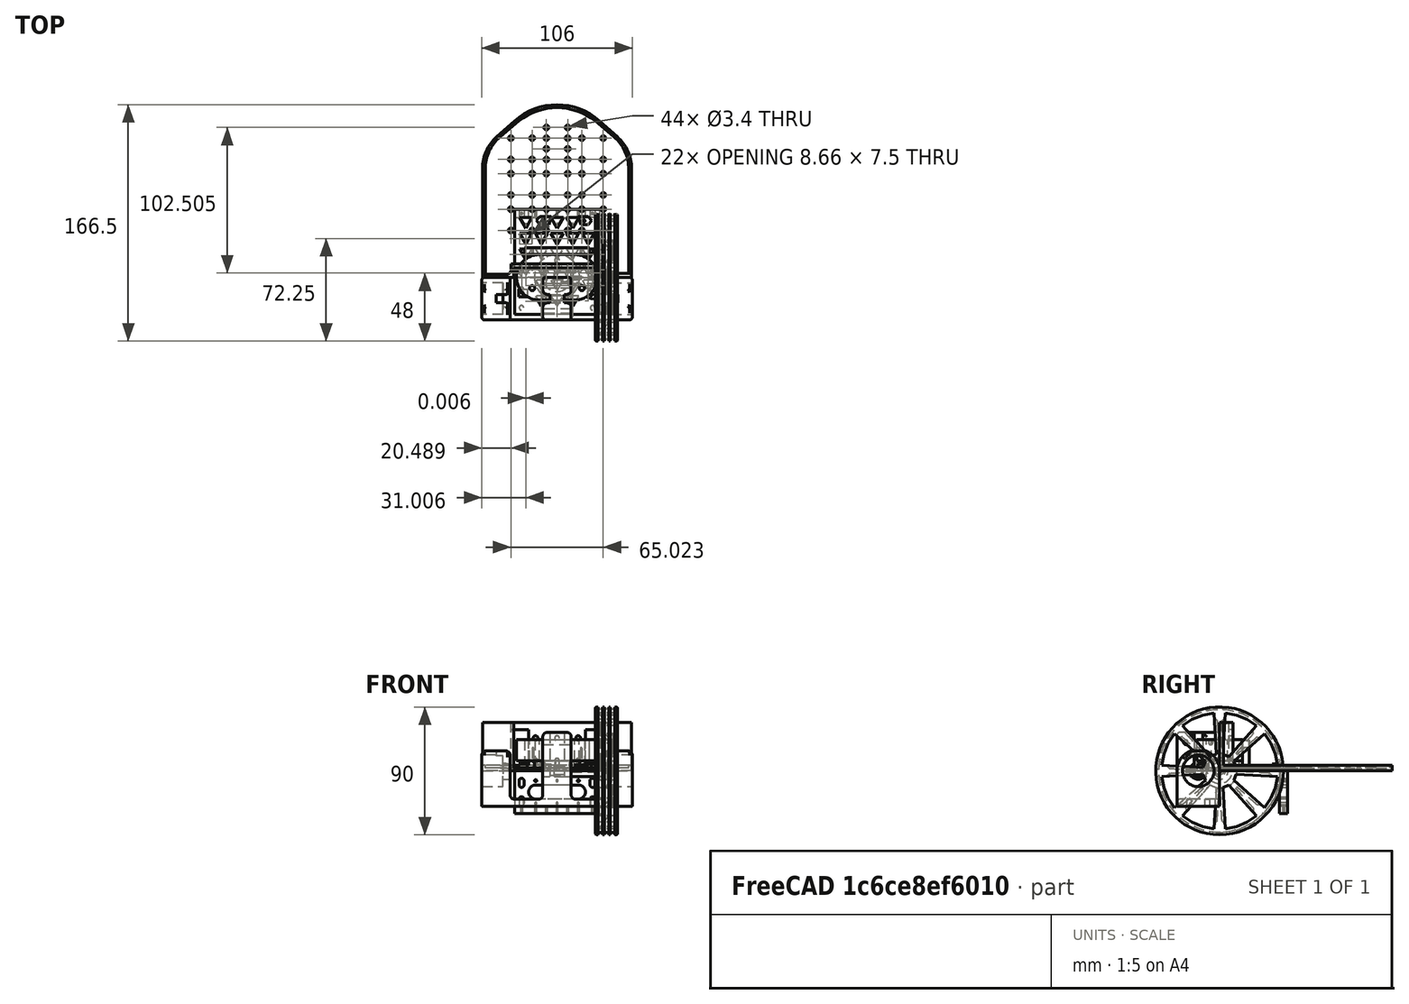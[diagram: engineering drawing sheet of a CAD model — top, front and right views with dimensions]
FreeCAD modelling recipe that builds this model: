
FCSTD DOCUMENT  (FreeCAD 0.18R4 (GitTag))
Label: MotoriGialliRuote90-r00
License: All rights reserved
LicenseURL: http://en.wikipedia.org/wiki/All_rights_reserved
objects: Sketcher::SketchObject×29, PartDesign::Pocket×17, PartDesign::Pad×11, PartDesign::Body×6, App::Part×6, PartDesign::Fillet×2, PartDesign::Revolution×1, PartDesign::FeatureBase×1, Mesh::Feature×1
note: 96 computed .brp shape members not serialized (recipe doc carries the construction recipe); baked Part::Feature solids carry a one-line shape summary decoded from their .brp

FEATURE [Sketcher::SketchObject] Sketch  label="ProfiloPrincipaleStaffa"
  MapMode = 5
  Placement = pos=(0,0,0) rot=(1,0,0;1.5708rad)
  Support = -> [XZ_Plane001]
  constraints (76):
    c: Vertical(g1)
    c: Horizontal(g2)
    c: Coincident(g3,g4)
    c: Horizontal(g4)
    c: Horizontal(g5)
    c: Vertical(g6)
    c: Equal(g5,g2)
    c: Vertical(g3)
    c: DistanceY(g3,g-1) = 20
    c: Horizontal(g7)
    c: DistanceX(g7,g7) = 20
    c: DistanceX(g7,g3) = 43
    c: Tangent(g0,g8) = 1.5708
    c: Tangent(g1,g8) = 1.5708
    c: Tangent(g0,g9) = 1.5708
    c: Tangent(g6,g9) = 1.5708
    c: Equal(g9,g8)
    c: Radius(g9) = 3
    c: DistanceY(g-1,g0) = 27
    c: Tangent(g5,g10) = -1.5708
    c: Tangent(g6,g10) = -1.5708
    c: Tangent(g1,g11) = -1.5708
    c: Tangent(g2,g11) = -1.5708
    c: Equal(g11,g10)
    c: Equal(g10,g9)
    c: Coincident(g7,g6)
    c: Coincident(g7,g1)
    c: Coincident(g12,g5)
    c: PointOnObject(g12,g4)
    c: Vertical(g12)
    c: DistanceY(g12,g5) = 5
    c: Vertical(g13)
    c: Horizontal(g14)
    c: Coincident(g15,g3)
    c: Vertical(g15)
    c: Tangent(g2,g16) = -1.5708
    c: Tangent(g13,g16) = -1.5708
    c: Equal(g16,g11)
    c: Coincident(g17,g1)
    c: Coincident(g17,g13)
    c: DistanceX(g17,g17) = 23
    c: Symmetric(g0,g0,g-2)
    c: Tangent(g13,g18) = 1.5708
    c: Tangent(g14,g18) = 1.5708
    c: Tangent(g14,g19) = 1.5708
    c: Tangent(g15,g19) = 1.5708
    c: Equal(g19,g18)
    c: Equal(g18,g16)
    c: Coincident(g20,g13)
    c: Coincident(g20,g15)
    c: Vertical(g21)
    c: Horizontal(g22)
    c: Vertical(g23)
    c: Coincident(g23,g24)
    c: Vertical(g24)
    c: Coincident(g24,g4)
    c: Tangent(g23,g25) = -1.5708
    c: Tangent(g22,g25) = -1.5708
    c: Tangent(g22,g26) = -1.5708
    c: Tangent(g21,g26) = -1.5708
    c: Tangent(g21,g27) = 1.5708
    c: Tangent(g5,g27) = -1.5708
    c: Equal(g27,g26)
    c: Equal(g26,g25)
    c: Equal(g25,g10)
    c: Coincident(g28,g21)
    c: Coincident(g28,g13)
    c: Horizontal(g28)
    c: Equal(g14,g22)
    c: Coincident(g29,g23)
    c: Coincident(g29,g5)
    c: Horizontal(g29)
    c: Coincident(g30,g2)
    c: Coincident(g30,g3)
    c: Horizontal(g30)
    c: DistanceY(g-1,g14) = 14
FEATURE [PartDesign::Pad] Pad  label="ProfiloPrincipaleStaffa001"
  Length = 30
  Length2 = 100
  Placement = pos=(0,0,0) rot=(1,0,0;1.5708rad)
  Profile = -> Sketch
  Type = 0
FEATURE [PartDesign::Pocket] Pocket  label="Unnamed001"
  Length = 100
  Length2 = 100
  Type = 0
FEATURE [Sketcher::SketchObject] Sketch002  label="Unnamed002"
FEATURE [PartDesign::Pocket] Pocket001  label="Unnamed003"
  Length = 100
  Length2 = 100
  Type = 0
FEATURE [Sketcher::SketchObject] Sketch003  label="Unnamed004"
FEATURE [PartDesign::Pocket] Pocket002  label="Unnamed005"
  Length = 100
  Length2 = 100
  Type = 0
FEATURE [Sketcher::SketchObject] Sketch001  label="ScontornoSupportoCuscinettiSX"
  MapMode = 5
  Placement = pos=(-53,0,0) rot=(0.707107,0,-0.707107;3.14159rad)
  Support = -> [Pocket002]
  constraints (97):
    c: Coincident(g0,g1)
    c: Coincident(g11,g2)
    c: Coincident(g2,g3)
    c: Coincident(g10,g0)
    c: Horizontal(g0)
    c: Horizontal(g2)
    c: Vertical(g1)
    c: Vertical(g3)
    c: Horizontal(g4)
    c: Coincident(g4,g5)
    c: Vertical(g5)
    c: Coincident(g5,g6)
    c: Horizontal(g6)
    c: Horizontal(g7)
    c: Coincident(g7,g8)
    c: Vertical(g8)
    c: Coincident(g8,g9)
    c: Equal(g8,g5)
    c: DistanceY(g8,g7) = 6
    c: Tangent(g3,g10)
    c: Tangent(g1,g11)
    c: Horizontal(g9)
    c: Tangent(g7,g12) = 1.5708
    c: Tangent(g10,g12) = -1.5708
    c: Tangent(g9,g13) = 1.5708
    c: Tangent(g3,g13) = -1.5708
    c: Tangent(g11,g14) = -1.5708
    c: Tangent(g6,g14) = -1.5708
    c: Tangent(g4,g15) = -1.5708
    c: Tangent(g1,g15) = -1.5708
    c: Equal(g15,g12)
    c: Equal(g12,g13)
    c: Radius(g12) = 3
    c: Equal(g10,g11)
    c: Equal(g11,g3)
    c: Equal(g1,g10)
    c: DistanceX(g0,g4) = 5
    c: DistanceX(g7,g0) = 10
    c: DistanceX(g2,g2) = 23
    c: DistanceX(g5,g-1) = 5
    c: Coincident(g16,g1)
    c: Coincident(g17,g16)
    c: Coincident(g17,g11)
    c: Vertical(g17)
    c: Equal(g17,g16)
    c: DistanceY(g-1,g16) = 15
    c: Coincident(g18,g19)
    c: Coincident(g29,g20)
    c: Coincident(g20,g21)
    c: Coincident(g28,g18)
    c: Horizontal(g18)
    c: Horizontal(g20)
    c: Vertical(g19)
    c: Vertical(g21)
    c: Horizontal(g22)
    c: Coincident(g22,g23)
    c: Vertical(g23)
    c: Coincident(g23,g24)
    c: Horizontal(g24)
    c: Horizontal(g25)
    c: Coincident(g25,g26)
    c: Vertical(g26)
    c: Coincident(g26,g27)
    c: Equal(g26,g23)
    c: Tangent(g21,g28)
    c: Tangent(g19,g29)
    c: Horizontal(g27)
    c: Tangent(g25,g30) = 1.5708
    c: Tangent(g28,g30) = -1.5708
    c: Tangent(g27,g31) = 1.5708
    c: Tangent(g21,g31) = -1.5708
    c: Tangent(g29,g32) = -1.5708
    c: Tangent(g24,g32) = -1.5708
    c: Tangent(g22,g33) = -1.5708
    c: Tangent(g19,g33) = -1.5708
    c: Equal(g33,g30)
    c: Equal(g30,g31)
    c: Radius(g30) = 3
    c: Equal(g28,g29)
    c: Equal(g29,g21)
    c: Equal(g19,g28)
    c: Coincident(g34,g19)
    c: Coincident(g35,g34)
    c: Coincident(g35,g29)
    c: Vertical(g35)
    c: Equal(g35,g34)
    c: Equal(g26,g5)
    c: Equal(g20,g0)
    c: Equal(g21,g1)
    c: DistanceY(g2,g0) = 20
    c: Coincident(g36,g16)
    c: PointOnObject(g36,g-2)
    c: Horizontal(g36)
    c: Coincident(g37,g36)
    c: Coincident(g37,g34)
    c: Horizontal(g37)
    c: Equal(g36,g37)
FEATURE [Sketcher::SketchObject] Sketch004  label="Unnamed006"
FEATURE [PartDesign::Pocket] Pocket003  label="StaffaMotori004"
  BaseFeature = -> Pocket002
  Length = 25
  Length2 = 100
  Placement = pos=(0,0,0) rot=(1,0,0;1.5708rad)
  Profile = -> Sketch004
  Type = 0
FEATURE [PartDesign::Fillet] Fillet  label="StaffaMotori005"
  Base = -> Pocket003 [Edge114,Edge123]
  BaseFeature = -> Pocket003
  Placement = pos=(0,0,0) rot=(1,0,0;1.5708rad)
  Radius = 2
FEATURE [PartDesign::Pocket] Pocket004  label="Unnamed007"
  Length = 100
  Length2 = 100
  Type = 0
FEATURE [Sketcher::SketchObject] Sketch005  label="ScassoSedeCuscinettiRuotaDX"
  MapMode = 5
  Placement = pos=(53,0,0) rot=(0.707107,0,0.707107;3.14159rad)
  Support = -> [Pocket004]
  sketch-geometry (1):
    g0: Circle CenterX=0 CenterY=15 CenterZ=0 NormalX=0 NormalY=0 NormalZ=1 AngleXU=0 Radius=11.1
  constraints (3):
    c: PointOnObject(g0,g-2)
    c: Radius(g0) = 11.1
    c: DistanceY(g-1,g0) = 15
FEATURE [Sketcher::SketchObject] Sketch006  label="Unnamed008"
FEATURE [PartDesign::Pocket] Pocket005  label="StaffaMotori007"
  BaseFeature = -> Pocket004
  Length = 15
  Length2 = 100
  Placement = pos=(0,0,0) rot=(1,0,0;1.5708rad)
  Profile = -> Sketch006
  Type = 0
FEATURE [PartDesign::Pocket] Pocket006  label="Unnamed009"
  Length = 100
  Length2 = 100
  Type = 0
FEATURE [Sketcher::SketchObject] Sketch007  label="ForoMozzoRuotaSX"
  MapMode = 5
  Placement = pos=(-38,0,0) rot=(0.707107,0,-0.707107;3.14159rad)
  Support = -> [Pocket006]
  sketch-geometry (1):
    g0: Circle CenterX=0 CenterY=15 CenterZ=0 NormalX=0 NormalY=0 NormalZ=1 AngleXU=0 Radius=6
  constraints (3):
    c: PointOnObject(g0,g-2)
    c: Radius(g0) = 6
    c: DistanceY(g-1,g0) = 15
FEATURE [Sketcher::SketchObject] Sketch008  label="Unnamed010"
FEATURE [PartDesign::Pocket] Pocket007  label="StaffaMotori009"
  BaseFeature = -> Pocket006
  Length = 10
  Length2 = 100
  Placement = pos=(0,0,0) rot=(1,0,0;1.5708rad)
  Profile = -> Sketch008
  Type = 0
FEATURE [PartDesign::Pocket] Pocket008  label="Unnamed011"
  Length = 100
  Length2 = 100
  Type = 0
FEATURE [Sketcher::SketchObject] Sketch009  label="ForiFissaggioStaffaMotori"
  MapMode = 5
  Placement = pos=(0,-1.3e-14,-20) rot=(0,0,1;3.14159rad)
  Support = -> [Pocket008]
  sketch-geometry (4):
    g0: Circle CenterX=-20 CenterY=6.25 CenterZ=0 NormalX=0 NormalY=0 NormalZ=1 AngleXU=0 Radius=1.6
    g1: LineSegment StartX=-20 StartY=15 StartZ=0 EndX=-20 EndY=6.25 EndZ=0
    g2: Circle CenterX=25 CenterY=21.5 CenterZ=0 NormalX=0 NormalY=0 NormalZ=1 AngleXU=0 Radius=1.6
    g3: Circle CenterX=-25 CenterY=8.5 CenterZ=0 NormalX=0 NormalY=0 NormalZ=1 AngleXU=0 Radius=1.6
  constraints (11):
    c: Coincident(g2,g0)
    c: Vertical(g2)
    c: Coincident(g3,g2)
    c: Vertical(g3)
    c: Equal(g2,g3)
    c: DistanceY(g-1,g2) = 15
    c: Coincident(g1,g3)
    c: DistanceY(g1,g0) = 17.5
    c: Equal(g0,g1)
    c: Radius(g0) = 1.6
    c: DistanceX(g1,g-1) = 20
FEATURE [Sketcher::SketchObject] Sketch010  label="Unnamed012"
FEATURE [PartDesign::Pocket] Pocket009  label="StaffaMotori011"
  BaseFeature = -> Pocket008
  Length = 7
  Length2 = 100
  Placement = pos=(0,0,0) rot=(1,0,0;1.5708rad)
  Profile = -> Sketch010
  Type = 0
FEATURE [PartDesign::Body] Body  label="StaffaMotori"
  Group = -> [Sketch,Pad,Sketch001,Pocket,Sketch002,Pocket001,Sketch003,Pocket002,Sketch004,Pocket003,Fillet,Sketch005,Pocket004,Sketch006,Pocket005,Sketch007,Pocket006,Sketch008,Pocket007,Sketch009,Pocket008,Sketch010,Pocket009]
  Origin = -> Origin001
  Tip = -> Pocket009
FEATURE [App::Part] Part  label="Staffa Motori"
  Group = -> [Body]
  Origin = -> Origin
  Placement = pos=(0,0,15) rot=(1,0,0;1.5708rad)
FEATURE [Sketcher::SketchObject] Sketch011  label="ProfiloCerchione90asse8"
  MapMode = 5
  Placement = pos=(0,0,0) rot=(1,0,0;1.5708rad)
  Support = -> [XZ_Plane003]
  constraints (107):
    c: Vertical(g0)
    c: Coincident(g0,g1)
    c: Horizontal(g1)
    c: Coincident(g1,g2)
    c: Vertical(g2)
    c: Coincident(g2,g3)
    c: Horizontal(g3)
    c: Vertical(g4)
    c: Coincident(g5,g6)
    c: Vertical(g6)
    c: Vertical(g7)
    c: Coincident(g7,g8)
    c: Vertical(g9)
    c: Horizontal(g10)
    c: Coincident(g0,g10)
    c: Equal(g12,g13)
    c: Equal(g13,g11)
    c: Radius(g11) = 1.6
    c: Coincident(g14,g11)
    c: Coincident(g15,g12)
    c: Coincident(g16,g12)
    c: Coincident(g16,g13)
    c: Coincident(g17,g11)
    c: Horizontal(g14)
    c: Equal(g17,g14)
    c: Horizontal(g17)
    c: Coincident(g17,g13)
    c: Equal(g17,g16)
    c: Equal(g16,g15)
    c: Horizontal(g16)
    c: Horizontal(g15)
    c: Tangent(g6,g18) = -1.5708
    c: Tangent(g14,g18) = -1.5708
    c: Tangent(g7,g19) = -1.5708
    c: Tangent(g15,g19) = -1.5708
    c: Equal(g19,g18)
    c: Radius(g18) = 1
    c: Coincident(g20,g11)
    c: Coincident(g20,g11)
    c: Coincident(g21,g13)
    c: Coincident(g21,g13)
    c: Horizontal(g21)
    c: Coincident(g22,g12)
    c: Coincident(g22,g12)
    c: Horizontal(g22)
    c: Horizontal(g20)
    c: PointOnObject(g11,g20)
    c: PointOnObject(g13,g21)
    c: PointOnObject(g12,g22)
    c: Equal(g14,g15)
    c: DistanceX(g6,g11) = 2
    c: Equal(g6,g7)
    c: Coincident(g23,g5)
    c: Coincident(g23,g7)
    c: Horizontal(g24)
    c: Tangent(g4,g25) = 1.5708
    c: Tangent(g5,g25) = 1.5708
    c: Tangent(g9,g26) = 1.5708
    c: Tangent(g8,g26) = 1.5708
    c: Coincident(g24,g5)
    c: Coincident(g24,g8)
    c: Coincident(g27,g4)
    c: Coincident(g27,g9)
    c: Radius(g25) = 5
    c: DistanceY(g14,g5) = 2
    c: Coincident(g28,g25)
    c: Coincident(g28,g4)
    c: Coincident(g29,g9)
    c: Coincident(g29,g26)
    c: Coincident(g30,g26)
    c: Coincident(g30,g7)
    c: Vertical(g30)
    c: Coincident(g31,g25)
    c: Coincident(g31,g5)
    c: Equal(g28,g29)
    c: Equal(g31,g30)
    c: DistanceY(g15,g26) = 9
    c: PointOnObject(g32,g9)
    c: Horizontal(g32)
    c: Radius(g33) = 3
    c: Coincident(g10,g33)
    c: PointOnObject(g10,g-1)
    c: PointOnObject(g33,g-1)
    c: Coincident(g9,g33)
    c: Coincident(g34,g33)
    c: Coincident(g34,g9)
    c: Vertical(g34)
    c: Coincident(g35,g33)
    c: Coincident(g35,g10)
    c: DistanceY(g15,g-1) = 45
    c: Tangent(g3,g36) = 1.5708
    c: Tangent(g4,g36) = 1.5708
    c: Radius(g36) = 3
    c: DistanceY(g0,g0) = 4.1
    c: DistanceY(g2,g0) = 6
    c: DistanceX(g0,g2) = 29
    c: DistanceX(g3,g3) = 2
    c: Coincident(g32,g4)
    c: Coincident(g10,g37)
    c: PointOnObject(g37,g-1)
    c: Coincident(g37,g38)
    c: Coincident(g38,g7)
    c: Vertical(g38)
    c: DistanceX(g0,g-1) = 2
    c: Coincident(g39,g36)
    c: Coincident(g39,g25)
    c: Radius(g39) = 16
FEATURE [PartDesign::Revolution] Revolution  label="RuoteDa90asse009"
  Angle = 360
  Axis = (1,0,0)
  Base = (0,0,0)
  Placement = pos=(0,0,0) rot=(1,0,0;1.5708rad)
  Profile = -> Sketch011
  ReferenceAxis = -> Sketch011 [H_Axis]
  Reversed = true
FEATURE [Sketcher::SketchObject] Sketch013  label="AllegerimentoRuota"
  MapMode = 5
  Placement = pos=(42.6,0,0) rot=(0.707107,0,0.707107;3.14159rad)
  Support = -> [Revolution]
  sketch-geometry (6):
    g0: ArcOfCircle CenterX=0 CenterY=-0.8 CenterZ=0 NormalX=0 NormalY=0 NormalZ=1 AngleXU=0 Radius=2.4 StartAngle=3.14159 EndAngle=6.28319
    g1: LineSegment StartX=2.4 StartY=0.8 StartZ=0 EndX=2.4 EndY=-0.8 EndZ=0
    g2: LineSegment StartX=0 StartY=0 StartZ=0 EndX=0 EndY=-0.8 EndZ=0
    g3: LineSegment StartX=11.7694 StartY=-2.34108 StartZ=0 EndX=11.7694 EndY=2.34108 EndZ=0
    g4: LineSegment StartX=9.97764 StartY=6.66684 StartZ=0 EndX=6.66684 EndY=9.97764 EndZ=0
    g5: LineSegment StartX=2.34108 StartY=11.7694 StartZ=0 EndX=-2.34108 EndY=11.7694 EndZ=0
  constraints (14):
    c: Tangent(g0,g3) = 1.5708
    c: Tangent(g0,g2) = -1.5708
    c: Tangent(g2,g1) = -1.5708
    c: Tangent(g3,g1) = 1.5708
    c: Vertical(g2)
    c: Equal(g0,g1)
    c: Radius(g0) = 2.4
    c: DistanceY(g1,g0) = 1.6
    c: Coincident(g4,g0)
    c: Vertical(g4)
    c: Coincident(g5,g4)
    c: Equal(g5,g4)
    c: Coincident(g5,g1)
    c: Coincident(g-1,g4)
FEATURE [Sketcher::SketchObject] Sketch017  label="Unnamed013"
FEATURE [PartDesign::Pocket] Pocket014  label="RuoteDa90asse014"
  BaseFeature = -> Revolution
  Length = 15000
  Length2 = 100
  Placement = pos=(0,0,0) rot=(1,0,0;1.5708rad)
  Profile = -> Sketch017
  Type = 0
FEATURE [PartDesign::Fillet] Fillet001  label="RuoteDa90asse015"
  Base = -> Pocket014 [Edge19,Edge21,Edge23,Edge25,Edge17,Edge27,Edge29,Edge31,Edge33,Edge35,Edge37,Edge39,Edge41,Edge11,Edge13,Edge15,Edge14,Edge18,Edge22,Edge26,Edge30,Edge34,Edge38,Edge10]
  BaseFeature = -> Pocket014
  Placement = pos=(0,0,0) rot=(1,0,0;1.5708rad)
  Radius = 2
FEATURE [PartDesign::Pocket] Pocket015  label="RuoteDa90asse016"
  BaseFeature = -> Fillet001
  Length = 12
  Length2 = 100
  Placement = pos=(0,0,0) rot=(1,0,0;1.5708rad)
  Profile = -> Sketch013
  Type = 0
FEATURE [PartDesign::FeatureBase] Clone
  BaseFeature = -> Pocket015
  Placement = pos=(0,0,0) rot=(1,0,0;1.5708rad)
FEATURE [PartDesign::Body] Body002
  BaseFeature = -> Pocket015
  Group = -> [Clone]
  Origin = -> Origin004
  Tip = -> Clone
FEATURE [App::Part] Part002  label="Ruote da 90 asse 8DX"
  Group = -> [Body002]
  Origin = -> Origin005
  Placement = pos=(27,0,0) rot=(0,0,1;0rad)
FEATURE [Sketcher::SketchObject] Sketch018  label="PortaArduinoSopraMotori001"
  MapMode = 5
  Support = -> [XY_Plane007]
  constraints (429):
    c: Coincident(g0,g1)
    c: Coincident(g1,g2)
    c: Coincident(g2,g3)
    c: Coincident(g3,g0)
    c: Horizontal(g2)
    c: Vertical(g1)
    c: Vertical(g3)
    c: Symmetric(g0,g0,g-2)
    c: DistanceX(g0,g0) = 60
    c: DistanceY(g1,g-1) = 26
    c: DistanceY(g1,g0) = 74
    c: Coincident(g4,g5)
    c: Coincident(g5,g6)
    c: Coincident(g6,g4)
    c: Equal(g4,g5)
    c: Equal(g4,g6)
    c: PointOnObject(g4,g7)
    c: PointOnObject(g5,g7)
    c: PointOnObject(g6,g7)
    c: Radius(g7) = 5
    c: Horizontal(g4)
    c: Coincident(g8,g9)
    c: Coincident(g9,g10)
    c: Coincident(g10,g8)
    c: Equal(g8,g9)
    c: Equal(g8,g10)
    c: PointOnObject(g8,g11)
    c: PointOnObject(g9,g11)
    c: PointOnObject(g10,g11)
    c: Equal(g7,g11) = 5
    c: Horizontal(g8)
    c: Coincident(g4,g12)
    c: Coincident(g8,g12)
    c: Distance(g12) = 11
    c: Angle(g12) = 0.000544822
    c: Coincident(g13,g14)
    c: Coincident(g14,g15)
    c: Coincident(g15,g13)
    c: Equal(g13,g14)
    c: Equal(g13,g15)
    c: PointOnObject(g13,g16)
    c: PointOnObject(g14,g16)
    c: PointOnObject(g15,g16)
    c: Equal(g7,g16) = 5
    c: Horizontal(g13)
    c: Coincident(g8,g17)
    c: Coincident(g13,g17)
    c: Equal(g12,g17)
    c: Parallel(g17,g12)
    c: Coincident(g18,g19)
    c: Coincident(g19,g20)
    c: Coincident(g20,g18)
    c: Equal(g18,g19)
    c: Equal(g18,g20)
    c: PointOnObject(g18,g21)
    c: PointOnObject(g19,g21)
    c: PointOnObject(g20,g21)
    c: Equal(g7,g21) = 5
    c: Horizontal(g18)
    c: Coincident(g13,g22)
    c: Coincident(g18,g22)
    c: Equal(g12,g22)
    c: Parallel(g22,g12)
    c: Coincident(g23,g24)
    c: Coincident(g24,g25)
    c: Coincident(g25,g23)
    c: Equal(g23,g24)
    c: Equal(g23,g25)
    c: PointOnObject(g23,g26)
    c: PointOnObject(g24,g26)
    c: PointOnObject(g25,g26)
    c: Equal(g7,g26) = 5
    c: Horizontal(g23)
    c: Coincident(g18,g27)
    c: Coincident(g23,g27)
    c: Equal(g12,g27)
    c: Parallel(g27,g12)
    c: Coincident(g28,g29)
    c: Coincident(g29,g30)
    c: Coincident(g30,g28)
    c: Equal(g28,g29)
    c: Equal(g28,g30)
    c: PointOnObject(g28,g31)
    c: PointOnObject(g29,g31)
    c: PointOnObject(g30,g31)
    c: Equal(g7,g31) = 5
    c: Horizontal(g28)
    c: Coincident(g4,g32)
    c: Coincident(g28,g32)
    c: Equal(g32,g12)
    c: Perpendicular(g32,g12)
    c: Coincident(g33,g34)
    c: Coincident(g34,g35)
    c: Coincident(g35,g33)
    c: Equal(g33,g34)
    c: Equal(g33,g35)
    c: PointOnObject(g33,g36)
    c: PointOnObject(g34,g36)
    c: PointOnObject(g35,g36)
    c: Equal(g7,g36) = 5
    c: Horizontal(g33)
    c: Coincident(g28,g37)
    c: Coincident(g33,g37)
    c: Equal(g12,g37)
    c: Parallel(g37,g12)
    c: Coincident(g38,g39)
    c: Coincident(g39,g40)
    c: Coincident(g40,g38)
    c: Equal(g38,g39)
    c: Equal(g38,g40)
    c: PointOnObject(g38,g41)
    c: PointOnObject(g39,g41)
    c: PointOnObject(g40,g41)
    c: Equal(g7,g41) = 5
    c: Horizontal(g38)
    c: Coincident(g33,g42)
    c: Coincident(g38,g42)
    c: Equal(g12,g42)
    c: Parallel(g42,g12)
    c: Coincident(g43,g44)
    c: Coincident(g44,g45)
    c: Coincident(g45,g43)
    c: Equal(g43,g44)
    c: Equal(g43,g45)
    c: PointOnObject(g43,g46)
    c: PointOnObject(g44,g46)
    c: PointOnObject(g45,g46)
    c: Equal(g7,g46) = 5
    c: Horizontal(g43)
    c: Coincident(g38,g47)
    c: Coincident(g43,g47)
    c: Equal(g12,g47)
    c: Parallel(g47,g12)
    c: Coincident(g48,g49)
    c: Coincident(g49,g50)
    c: Coincident(g50,g48)
    c: Equal(g48,g49)
    c: Equal(g48,g50)
    c: PointOnObject(g48,g51)
    c: PointOnObject(g49,g51)
    c: PointOnObject(g50,g51)
    c: Equal(g7,g51) = 5
    c: Horizontal(g48)
    c: Coincident(g43,g52)
    c: Coincident(g48,g52)
    c: Equal(g12,g52)
    c: Parallel(g52,g12)
    c: Coincident(g53,g54)
    c: Coincident(g54,g55)
    c: Coincident(g55,g53)
    c: Equal(g53,g54)
    c: Equal(g53,g55)
    c: PointOnObject(g53,g56)
    c: PointOnObject(g54,g56)
    c: PointOnObject(g55,g56)
    c: Equal(g7,g56) = 5
    c: Horizontal(g53)
    c: Coincident(g28,g57)
    c: Coincident(g53,g57)
    c: Equal(g32,g57)
    c: Perpendicular(g57,g12)
    c: Coincident(g58,g59)
    c: Coincident(g59,g60)
    c: Coincident(g60,g58)
    c: Equal(g58,g59)
    c: Equal(g58,g60)
    c: PointOnObject(g58,g61)
    c: PointOnObject(g59,g61)
    c: PointOnObject(g60,g61)
    c: Equal(g7,g61) = 5
    c: Horizontal(g58)
    c: Coincident(g53,g62)
    c: Coincident(g58,g62)
    c: Equal(g12,g62)
    c: Parallel(g62,g12)
    c: Coincident(g63,g64)
    c: Coincident(g64,g65)
    c: Coincident(g65,g63)
    c: Equal(g63,g64)
    c: Equal(g63,g65)
    c: PointOnObject(g63,g66)
    c: PointOnObject(g64,g66)
    c: PointOnObject(g65,g66)
    c: Equal(g7,g66) = 5
    c: Horizontal(g63)
    c: Coincident(g58,g67)
    c: Coincident(g63,g67)
    c: Equal(g12,g67)
    c: Parallel(g67,g12)
    c: Coincident(g68,g69)
    c: Coincident(g69,g70)
    c: Coincident(g70,g68)
    c: Equal(g68,g69)
    c: Equal(g68,g70)
    c: PointOnObject(g68,g71)
    c: PointOnObject(g69,g71)
    c: PointOnObject(g70,g71)
    c: Equal(g7,g71) = 5
    c: Horizontal(g68)
    c: Coincident(g63,g72)
    c: Coincident(g68,g72)
    c: Equal(g12,g72)
    c: Parallel(g72,g12)
    c: Coincident(g73,g74)
    c: Coincident(g74,g75)
    c: Coincident(g75,g73)
    c: Equal(g73,g74)
    c: Equal(g73,g75)
    c: PointOnObject(g73,g76)
    c: PointOnObject(g74,g76)
    c: PointOnObject(g75,g76)
    c: Equal(g7,g76) = 5
    c: Horizontal(g73)
    c: Coincident(g68,g77)
    c: Coincident(g73,g77)
    c: Equal(g12,g77)
    c: Parallel(g77,g12)
    c: Coincident(g78,g79)
    c: Coincident(g79,g80)
    c: Coincident(g80,g78)
    c: Equal(g78,g79)
    c: Equal(g78,g80)
    c: PointOnObject(g78,g81)
    c: PointOnObject(g79,g81)
    c: PointOnObject(g80,g81)
    c: Equal(g7,g81) = 5
    c: Horizontal(g78)
    c: Coincident(g53,g82)
    c: Coincident(g78,g82)
    c: Equal(g32,g82)
    c: Perpendicular(g82,g12)
    c: Coincident(g83,g84)
    c: Coincident(g84,g85)
    c: Coincident(g85,g83)
    c: Equal(g83,g84)
    c: Equal(g83,g85)
    c: PointOnObject(g83,g86)
    c: PointOnObject(g84,g86)
    c: PointOnObject(g85,g86)
    c: Equal(g7,g86) = 5
    c: Horizontal(g83)
    c: Coincident(g78,g87)
    c: Coincident(g83,g87)
    c: Equal(g12,g87)
    c: Parallel(g87,g12)
    c: Coincident(g88,g89)
    c: Coincident(g89,g90)
    c: Coincident(g90,g88)
    c: Equal(g88,g89)
    c: Equal(g88,g90)
    c: PointOnObject(g88,g91)
    c: PointOnObject(g89,g91)
    c: PointOnObject(g90,g91)
    c: Equal(g7,g91) = 5
    c: Horizontal(g88)
    c: Coincident(g83,g92)
    c: Coincident(g88,g92)
    c: Equal(g12,g92)
    c: Parallel(g92,g12)
    c: Coincident(g93,g94)
    c: Coincident(g94,g95)
    c: Coincident(g95,g93)
    c: Equal(g93,g94)
    c: Equal(g93,g95)
    c: PointOnObject(g93,g96)
    c: PointOnObject(g94,g96)
    c: PointOnObject(g95,g96)
    c: Equal(g7,g96) = 5
    c: Horizontal(g93)
    c: Coincident(g88,g97)
    c: Coincident(g93,g97)
    c: Equal(g12,g97)
    c: Parallel(g97,g12)
    c: Coincident(g98,g99)
    c: Coincident(g99,g100)
    c: Coincident(g100,g98)
    c: Equal(g98,g99)
    c: Equal(g98,g100)
    c: PointOnObject(g98,g101)
    c: PointOnObject(g99,g101)
    c: PointOnObject(g100,g101)
    c: Equal(g7,g101) = 5
    c: Horizontal(g98)
    c: Coincident(g93,g102)
    c: Coincident(g98,g102)
    c: Equal(g12,g102)
    c: Parallel(g102,g12)
    c: Coincident(g103,g104)
    c: Coincident(g104,g105)
    c: Coincident(g105,g103)
    c: Equal(g103,g104)
    c: Equal(g103,g105)
    c: PointOnObject(g103,g106)
    c: PointOnObject(g104,g106)
    c: PointOnObject(g105,g106)
    c: Equal(g7,g106) = 5
    c: Horizontal(g103)
    c: Coincident(g78,g107)
    c: Coincident(g103,g107)
    c: Equal(g32,g107)
    c: Perpendicular(g107,g12)
    c: Coincident(g108,g109)
    c: Coincident(g109,g110)
    c: Coincident(g110,g108)
    c: Equal(g108,g109)
    c: Equal(g108,g110)
    c: PointOnObject(g108,g111)
    c: PointOnObject(g109,g111)
    c: PointOnObject(g110,g111)
    c: Equal(g7,g111) = 5
    c: Horizontal(g108)
    c: Coincident(g103,g112)
    c: Coincident(g108,g112)
    c: Equal(g12,g112)
    c: Parallel(g112,g12)
    c: Coincident(g113,g114)
    c: Coincident(g114,g115)
    c: Coincident(g115,g113)
    c: Equal(g113,g114)
    c: Equal(g113,g115)
    c: PointOnObject(g113,g116)
    c: PointOnObject(g114,g116)
    c: PointOnObject(g115,g116)
    c: Equal(g7,g116) = 5
    c: Horizontal(g113)
    c: Coincident(g108,g117)
    c: Coincident(g113,g117)
    c: Equal(g12,g117)
    c: Parallel(g117,g12)
    c: Coincident(g118,g119)
    c: Coincident(g119,g120)
    c: Coincident(g120,g118)
    c: Equal(g118,g119)
    c: Equal(g118,g120)
    c: PointOnObject(g118,g121)
    c: PointOnObject(g119,g121)
    c: PointOnObject(g120,g121)
    c: Equal(g7,g121) = 5
    c: Horizontal(g118)
    c: Coincident(g113,g122)
    c: Coincident(g118,g122)
    c: Equal(g12,g122)
    c: Parallel(g122,g12)
    c: Coincident(g123,g124)
    c: Coincident(g124,g125)
    c: Coincident(g125,g123)
    c: Equal(g123,g124)
    c: Equal(g123,g125)
    c: PointOnObject(g123,g126)
    c: PointOnObject(g124,g126)
    c: PointOnObject(g125,g126)
    c: Equal(g7,g126) = 5
    c: Horizontal(g123)
    c: Coincident(g118,g127)
    c: Coincident(g123,g127)
    c: Equal(g12,g127)
    c: Parallel(g127,g12)
    c: Coincident(g128,g129)
    c: Coincident(g129,g130)
    c: Coincident(g130,g128)
    c: Equal(g128,g129)
    c: Equal(g128,g130)
    c: PointOnObject(g128,g131)
    c: PointOnObject(g129,g131)
    c: PointOnObject(g130,g131)
    c: Equal(g7,g131) = 5
    c: Horizontal(g128)
    c: Coincident(g103,g132)
    c: Coincident(g128,g132)
    c: Equal(g32,g132)
    c: Perpendicular(g132,g12)
    c: Coincident(g133,g134)
    c: Coincident(g134,g135)
    c: Coincident(g135,g133)
    c: Equal(g133,g134)
    c: Equal(g133,g135)
    c: PointOnObject(g133,g136)
    c: PointOnObject(g134,g136)
    c: PointOnObject(g135,g136)
    c: Equal(g7,g136) = 5
    c: Horizontal(g133)
    c: Coincident(g128,g137)
    c: Coincident(g133,g137)
    c: Equal(g12,g137)
    c: Parallel(g137,g12)
    c: Coincident(g138,g139)
    c: Coincident(g139,g140)
    c: Coincident(g140,g138)
    c: Equal(g138,g139)
    c: Equal(g138,g140)
    c: PointOnObject(g138,g141)
    c: PointOnObject(g139,g141)
    c: PointOnObject(g140,g141)
    c: Equal(g7,g141) = 5
    c: Horizontal(g138)
    c: Coincident(g133,g142)
    c: Coincident(g138,g142)
    c: Equal(g12,g142)
    c: Parallel(g142,g12)
    c: Coincident(g143,g144)
    c: Coincident(g144,g145)
    c: Coincident(g145,g143)
    c: Equal(g143,g144)
    c: Equal(g143,g145)
    c: PointOnObject(g143,g146)
    c: PointOnObject(g144,g146)
    c: PointOnObject(g145,g146)
    c: Equal(g7,g146) = 5
    c: Horizontal(g143)
    c: Coincident(g138,g147)
    c: Coincident(g143,g147)
    c: Equal(g12,g147)
    c: Parallel(g147,g12)
    c: Coincident(g148,g149)
    c: Coincident(g149,g150)
    c: Coincident(g150,g148)
    c: Equal(g148,g149)
    c: Equal(g148,g150)
    c: PointOnObject(g148,g151)
    c: PointOnObject(g149,g151)
    c: PointOnObject(g150,g151)
    c: Equal(g7,g151) = 5
    c: Horizontal(g148)
    c: Coincident(g143,g152)
    c: Coincident(g148,g152)
    c: Equal(g12,g152)
    c: Parallel(g152,g12)
    c: PointOnObject(g14,g-2)
    c: DistanceY(g4,g0) = 6
FEATURE [Mesh::Feature] Arduino_ipt  label="Arduino.ipt"
  Placement = pos=(35,0,38) rot=(0,0,1;0rad)
FEATURE [PartDesign::Pad] Pad001  label="PortaArduinoSopraMotori002"
  Length = 2
  Length2 = 100
  Profile = -> Sketch018
  Type = 0
FEATURE [PartDesign::Pad] Pad002  label="Unnamed014"
  Length = 100
  Length2 = 100
  Type = 0
FEATURE [Sketcher::SketchObject] Sketch020  label="Unnamed015"
FEATURE [PartDesign::Pad] Pad003  label="Unnamed016"
  Length = 100
  Length2 = 100
  Type = 0
FEATURE [Sketcher::SketchObject] Sketch019  label="ForiSupportoMotoriPiuStaffaTimone"
  MapMode = 5
  Placement = pos=(0,48,0) rot=(0,0.707107,0.707107;3.14159rad)
  Support = -> [Pad003]
  constraints (94):
    c: Vertical(g0)
    c: Vertical(g1)
    c: Coincident(g2,g3)
    c: Horizontal(g3)
    c: Coincident(g3,g4)
    c: Horizontal(g5)
    c: Coincident(g6,g7)
    c: Horizontal(g7)
    c: Coincident(g23,g2)
    c: Coincident(g1,g7)
    c: Coincident(g8,g0)
    c: Coincident(g8,g24)
    c: Coincident(g3,g9)
    c: Coincident(g9,g10)
    c: Horizontal(g10)
    c: Coincident(g10,g11)
    c: Coincident(g11,g12)
    c: PointOnObject(g12,g5)
    c: Coincident(g12,g13)
    c: Coincident(g13,g14)
    c: Horizontal(g14)
    c: Coincident(g14,g15)
    c: Coincident(g15,g6)
    c: Horizontal(g16)
    c: Coincident(g16,g17)
    c: Vertical(g17)
    c: Coincident(g17,g18)
    c: Horizontal(g19)
    c: Coincident(g19,g20)
    c: Vertical(g20)
    c: Coincident(g20,g21)
    c: Coincident(g21,g22)
    c: Coincident(g5,g11)
    c: PointOnObject(g5,g13)
    c: Coincident(g0,g18)
    c: Coincident(g23,g16)
    c: Tangent(g0,g23)
    c: Coincident(g1,g19)
    c: Coincident(g24,g22)
    c: Tangent(g1,g24)
    c: Coincident(g25,g4)
    c: Coincident(g25,g5)
    c: Horizontal(g25)
    c: Coincident(g26,g5)
    c: Coincident(g26,g6)
    c: Horizontal(g26)
    c: Coincident(g27,g16)
    c: Coincident(g27,g0)
    c: Coincident(g28,g1)
    c: Coincident(g28,g22)
    c: Horizontal(g18)
    c: DistanceX(g4,g6) = 34
    c: DistanceX(g5,g5) = 19
    c: DistanceX(g25,g25) = 8
    c: DistanceX(g4,g-1) = 12
    c: Coincident(g29,g4)
    c: Coincident(g29,g9)
    c: Vertical(g29)
    c: Coincident(g30,g6)
    c: Coincident(g30,g14)
    c: Vertical(g30)
    c: Coincident(g31,g10)
    c: Horizontal(g31)
    c: Coincident(g32,g31)
    c: Horizontal(g32)
    c: Coincident(g33,g32)
    c: Coincident(g33,g13)
    c: Horizontal(g33)
    c: Coincident(g34,g5)
    c: Coincident(g34,g31)
    c: Vertical(g34)
    c: Coincident(g35,g5)
    c: Coincident(g35,g32)
    c: Vertical(g35)
    c: DistanceX(g10,g13) = 22.5
    c: Equal(g31,g33)
    c: DistanceX(g3,g4) = 2.5
    c: DistanceX(g6,g7) = 2.5
    c: DistanceX(g0,g8) = 54
    c: Symmetric(g0,g8,g-2)
    c: Equal(g36,g37)
    c: Equal(g37,g39)
    c: Equal(g39,g38)
    c: Radius(g38) = 0.75
    c: Coincident(g40,g36)
    c: Coincident(g40,g37)
    c: Horizontal(g40)
    c: DistanceX(g40,g40) = 27.75
    c: DistanceX(g36,g-1) = 8.75
    c: DistanceY(g36,g2) = 0.5
    c: DistanceX(g0,g38) = 3
    c: DistanceY(g38,g-1) = 11
    c: DistanceX(g39,g1) = 2.75
    c: DistanceY(g39,g-1) = 12.25
FEATURE [Sketcher::SketchObject] Sketch021  label="Unnamed017"
FEATURE [PartDesign::Pocket] Pocket016  label="PortaArduinoSopraMotori005"
  BaseFeature = -> Pad003
  Length = 7
  Length2 = 100
  Profile = -> Sketch021
  Type = 0
FEATURE [Sketcher::SketchObject] Sketch022  label="ForiFissaggioTimone"
  MapMode = 5
  Placement = pos=(0,0,-30) rot=(1,0,0;3.14159rad)
  Support = -> [Pocket016]
  constraints (30):
    c: Horizontal(g0)
    c: Coincident(g1,g0)
    c: Horizontal(g1)
    c: Coincident(g2,g1)
    c: Coincident(g3,g2)
    c: Horizontal(g3)
    c: Coincident(g4,g3)
    c: Horizontal(g4)
    c: Coincident(g5,g0)
    c: Coincident(g6,g0)
    c: Coincident(g7,g1)
    c: PointOnObject(g8,g-2)
    c: Coincident(g9,g2)
    c: Coincident(g10,g3)
    c: Coincident(g11,g4)
    c: PointOnObject(g8,g2)
    c: Equal(g10,g9)
    c: Equal(g9,g11)
    c: Equal(g11,g8)
    c: Equal(g8,g7)
    c: Equal(g7,g6)
    c: Equal(g6,g5)
    c: Radius(g5) = 0.75
    c: Symmetric(g7,g9,g-2)
    c: Equal(g1,g3)
    c: Equal(g0,g4)
    c: DistanceY(g5,g-1) = 45
    c: DistanceX(g5,g-1) = 25
    c: DistanceX(g-1,g10) = 15
    c: DistanceX(g-1,g9) = 7.5
FEATURE [PartDesign::Pocket] Pocket017  label="PortaArduinoSopraMotori006"
  BaseFeature = -> Pocket016
  Length = 5
  Length2 = 100
  Profile = -> Sketch022
  Type = 0
FEATURE [PartDesign::Body] Body003  label="PortaArduinoSopraMotori"
  Group = -> [Sketch018,Pad001,Sketch019,Pad002,Sketch020,Pad003,Sketch021,Pocket016,Sketch022,Pocket017]
  Origin = -> Origin007
  Tip = -> Pocket017
FEATURE [App::Part] Part003  label="Porta Arduino Sopra Motori"
  Group = -> [Body003,Arduino_ipt]
  Origin = -> Origin006
  Placement = pos=(0,-17,15) rot=(0,0,1;0rad)
FEATURE [Sketcher::SketchObject] Sketch023  label="TimonePortaBatterie002"
  MapMode = 5
  Support = -> [XY_Plane009]
  sketch-geometry (114):
    g0: LineSegment StartX=-52.5 StartY=0 StartZ=0 EndX=-30.5 EndY=0 EndZ=0
    g1: LineSegment [constr] StartX=-30.5 StartY=0 StartZ=0 EndX=-30.5 EndY=6.5 EndZ=0
    g2: LineSegment [constr] StartX=-30.5 StartY=6.5 StartZ=0 EndX=30.5 EndY=6.5 EndZ=0
    g3: LineSegment [constr] StartX=30.5 StartY=6.5 StartZ=0 EndX=30.5 EndY=0 EndZ=0
    g4: LineSegment StartX=30.5 StartY=0 StartZ=0 EndX=52.5 EndY=0 EndZ=0
    g5: LineSegment StartX=52.5 StartY=0 StartZ=0 EndX=52.5 EndY=76.5 EndZ=0
    g6: LineSegment StartX=42.5 StartY=98.8607 StartZ=0 EndX=30 EndY=110.041 EndZ=0
    g7: LineSegment StartX=-30 StartY=110.041 StartZ=0 EndX=-42.5 EndY=98.8607 EndZ=0
    g8: LineSegment StartX=-52.5 StartY=76.5 StartZ=0 EndX=-52.5 EndY=0 EndZ=0
    g9: ArcOfCircle CenterX=0 CenterY=76.5 CenterZ=0 NormalX=0 NormalY=0 NormalZ=1 AngleXU=0 Radius=45 StartAngle=0.841069 EndAngle=2.30052
    g10: LineSegment [constr] StartX=-30 StartY=110.041 StartZ=0 EndX=30 EndY=110.041 EndZ=0
    g11: ArcOfCircle CenterX=-22.5 CenterY=76.5 CenterZ=0 NormalX=0 NormalY=0 NormalZ=1 AngleXU=0 Radius=30 StartAngle=2.30052 EndAngle=3.14159
    g12: ArcOfCircle CenterX=22.5 CenterY=76.5 CenterZ=0 NormalX=0 NormalY=0 NormalZ=1 AngleXU=0 Radius=30 StartAngle=0 EndAngle=0.841069
    g13: LineSegment [constr] StartX=-52.5 StartY=76.5 StartZ=0 EndX=52.5 EndY=76.5 EndZ=0
    g14: LineSegment [constr] StartX=-42.5 StartY=98.8607 StartZ=0 EndX=42.5 EndY=98.8607 EndZ=0
    g15: LineSegment [constr] StartX=-52.5 StartY=76.5 StartZ=0 EndX=-52.5 EndY=121.5 EndZ=0
    g16: LineSegment [constr] StartX=-52.5 StartY=121.5 StartZ=0 EndX=52.5 EndY=121.5 EndZ=0
    g17: LineSegment [constr] StartX=52.5 StartY=121.5 StartZ=0 EndX=52.5 EndY=76.5 EndZ=0
    g18: Circle CenterX=17.5115 CenterY=32.9821 CenterZ=0 NormalX=0 NormalY=0 NormalZ=1 AngleXU=0 Radius=1.7
    g19: Circle CenterX=17.5115 CenterY=47.9821 CenterZ=0 NormalX=0 NormalY=0 NormalZ=1 AngleXU=0 Radius=1.7
    g20: Circle CenterX=32.5115 CenterY=47.9821 CenterZ=0 NormalX=0 NormalY=0 NormalZ=1 AngleXU=0 Radius=1.7
    g21: Circle CenterX=32.5115 CenterY=32.9821 CenterZ=0 NormalX=0 NormalY=0 NormalZ=1 AngleXU=0 Radius=1.7
    g22: LineSegment [constr] StartX=17.5115 StartY=47.9821 StartZ=0 EndX=32.5115 EndY=47.9821 EndZ=0
    g23: LineSegment [constr] StartX=32.5115 StartY=47.9821 StartZ=0 EndX=32.5115 EndY=32.9821 EndZ=0
    g24: LineSegment [constr] StartX=32.5115 StartY=32.9821 StartZ=0 EndX=17.5115 EndY=32.9821 EndZ=0
    g25: LineSegment [constr] StartX=17.5115 StartY=32.9821 StartZ=0 EndX=17.5115 EndY=47.9821 EndZ=0
    g26: Circle CenterX=-7.5 CenterY=32.9821 CenterZ=0 NormalX=0 NormalY=0 NormalZ=1 AngleXU=0 Radius=1.7
    g27: Circle CenterX=-7.5 CenterY=47.9821 CenterZ=0 NormalX=0 NormalY=0 NormalZ=1 AngleXU=0 Radius=1.7
    g28: Circle CenterX=7.5 CenterY=47.9821 CenterZ=0 NormalX=0 NormalY=0 NormalZ=1 AngleXU=0 Radius=1.7
    g29: Circle CenterX=7.5 CenterY=32.9821 CenterZ=0 NormalX=0 NormalY=0 NormalZ=1 AngleXU=0 Radius=1.7
    g30: LineSegment [constr] StartX=-7.5 StartY=47.9821 StartZ=0 EndX=7.5 EndY=47.9821 EndZ=0
    g31: LineSegment [constr] StartX=7.5 StartY=47.9821 StartZ=0 EndX=7.5 EndY=32.9821 EndZ=0
    g32: LineSegment [constr] StartX=7.5 StartY=32.9821 StartZ=0 EndX=-7.5 EndY=32.9821 EndZ=0
    g33: LineSegment [constr] StartX=-7.5 StartY=32.9821 StartZ=0 EndX=-7.5 EndY=47.9821 EndZ=0
    g34: LineSegment [constr] StartX=17.5115 StartY=32.9821 StartZ=0 EndX=-7.5 EndY=32.9821 EndZ=0
    g35: Circle CenterX=-32.5115 CenterY=32.9821 CenterZ=0 NormalX=0 NormalY=0 NormalZ=1 AngleXU=0 Radius=1.7
    g36: Circle CenterX=-32.5115 CenterY=47.9821 CenterZ=0 NormalX=0 NormalY=0 NormalZ=1 AngleXU=0 Radius=1.7
    g37: Circle CenterX=-17.5115 CenterY=47.9821 CenterZ=0 NormalX=0 NormalY=0 NormalZ=1 AngleXU=0 Radius=1.7
    g38: Circle CenterX=-17.5115 CenterY=32.9821 CenterZ=0 NormalX=0 NormalY=0 NormalZ=1 AngleXU=0 Radius=1.7
    g39: LineSegment [constr] StartX=-32.5115 StartY=47.9821 StartZ=0 EndX=-17.5115 EndY=47.9821 EndZ=0
    g40: LineSegment [constr] StartX=-17.5115 StartY=47.9821 StartZ=0 EndX=-17.5115 EndY=32.9821 EndZ=0
    g41: LineSegment [constr] StartX=-17.5115 StartY=32.9821 StartZ=0 EndX=-32.5115 EndY=32.9821 EndZ=0
    g42: LineSegment [constr] StartX=-32.5115 StartY=32.9821 StartZ=0 EndX=-32.5115 EndY=47.9821 EndZ=0
    g43: LineSegment [constr] StartX=-7.5 StartY=32.9821 StartZ=0 EndX=-32.5115 EndY=32.9821 EndZ=0
    g44: Circle CenterX=17.5115 CenterY=57.9936 CenterZ=0 NormalX=0 NormalY=0 NormalZ=1 AngleXU=0 Radius=1.7
    g45: Circle CenterX=17.5115 CenterY=72.9936 CenterZ=0 NormalX=0 NormalY=0 NormalZ=1 AngleXU=0 Radius=1.7
    g46: Circle CenterX=32.5115 CenterY=72.9936 CenterZ=0 NormalX=0 NormalY=0 NormalZ=1 AngleXU=0 Radius=1.7
    g47: Circle CenterX=32.5115 CenterY=57.9936 CenterZ=0 NormalX=0 NormalY=0 NormalZ=1 AngleXU=0 Radius=1.7
    g48: LineSegment [constr] StartX=17.5115 StartY=72.9936 StartZ=0 EndX=32.5115 EndY=72.9936 EndZ=0
    g49: LineSegment [constr] StartX=32.5115 StartY=72.9936 StartZ=0 EndX=32.5115 EndY=57.9936 EndZ=0
    g50: LineSegment [constr] StartX=32.5115 StartY=57.9936 StartZ=0 EndX=17.5115 EndY=57.9936 EndZ=0
    g51: LineSegment [constr] StartX=17.5115 StartY=57.9936 StartZ=0 EndX=17.5115 EndY=72.9936 EndZ=0
    g52: LineSegment [constr] StartX=17.5115 StartY=32.9821 StartZ=0 EndX=17.5115 EndY=57.9936 EndZ=0
    g53: Circle CenterX=-7.5 CenterY=57.9936 CenterZ=0 NormalX=0 NormalY=0 NormalZ=1 AngleXU=0 Radius=1.7
    g54: Circle CenterX=-7.5 CenterY=72.9936 CenterZ=0 NormalX=0 NormalY=0 NormalZ=1 AngleXU=0 Radius=1.7
    g55: Circle CenterX=7.5 CenterY=72.9936 CenterZ=0 NormalX=0 NormalY=0 NormalZ=1 AngleXU=0 Radius=1.7
    g56: Circle CenterX=7.5 CenterY=57.9936 CenterZ=0 NormalX=0 NormalY=0 NormalZ=1 AngleXU=0 Radius=1.7
    g57: LineSegment [constr] StartX=-7.5 StartY=72.9936 StartZ=0 EndX=7.5 EndY=72.9936 EndZ=0
    g58: LineSegment [constr] StartX=7.5 StartY=72.9936 StartZ=0 EndX=7.5 EndY=57.9936 EndZ=0
    g59: LineSegment [constr] StartX=7.5 StartY=57.9936 StartZ=0 EndX=-7.5 EndY=57.9936 EndZ=0
    g60: LineSegment [constr] StartX=-7.5 StartY=57.9936 StartZ=0 EndX=-7.5 EndY=72.9936 EndZ=0
    g61: LineSegment [constr] StartX=17.5115 StartY=57.9936 StartZ=0 EndX=-7.5 EndY=57.9936 EndZ=0
    g62: Circle CenterX=-32.5115 CenterY=57.9936 CenterZ=0 NormalX=0 NormalY=0 NormalZ=1 AngleXU=0 Radius=1.7
    g63: Circle CenterX=-32.5115 CenterY=72.9936 CenterZ=0 NormalX=0 NormalY=0 NormalZ=1 AngleXU=0 Radius=1.7
    g64: Circle CenterX=-17.5115 CenterY=72.9936 CenterZ=0 NormalX=0 NormalY=0 NormalZ=1 AngleXU=0 Radius=1.7
    g65: Circle CenterX=-17.5115 CenterY=57.9936 CenterZ=0 NormalX=0 NormalY=0 NormalZ=1 AngleXU=0 Radius=1.7
    g66: LineSegment [constr] StartX=-32.5115 StartY=72.9936 StartZ=0 EndX=-17.5115 EndY=72.9936 EndZ=0
    g67: LineSegment [constr] StartX=-17.5115 StartY=72.9936 StartZ=0 EndX=-17.5115 EndY=57.9936 EndZ=0
    g68: LineSegment [constr] StartX=-17.5115 StartY=57.9936 StartZ=0 EndX=-32.5115 EndY=57.9936 EndZ=0
    g69: LineSegment [constr] StartX=-32.5115 StartY=57.9936 StartZ=0 EndX=-32.5115 EndY=72.9936 EndZ=0
    g70: LineSegment [constr] StartX=-7.5 StartY=57.9936 StartZ=0 EndX=-32.5115 EndY=57.9936 EndZ=0
    g71: Circle CenterX=17.5115 CenterY=83.0051 CenterZ=0 NormalX=0 NormalY=0 NormalZ=1 AngleXU=0 Radius=1.7
    g72: Circle CenterX=17.5115 CenterY=98.0051 CenterZ=0 NormalX=0 NormalY=0 NormalZ=1 AngleXU=0 Radius=1.7
    g73: Circle CenterX=32.5115 CenterY=98.0051 CenterZ=0 NormalX=0 NormalY=0 NormalZ=1 AngleXU=0 Radius=1.7
    g74: Circle CenterX=32.5115 CenterY=83.0051 CenterZ=0 NormalX=0 NormalY=0 NormalZ=1 AngleXU=0 Radius=1.7
    g75: LineSegment [constr] StartX=17.5115 StartY=98.0051 StartZ=0 EndX=32.5115 EndY=98.0051 EndZ=0
    g76: LineSegment [constr] StartX=32.5115 StartY=98.0051 StartZ=0 EndX=32.5115 EndY=83.0051 EndZ=0
    g77: LineSegment [constr] StartX=32.5115 StartY=83.0051 StartZ=0 EndX=17.5115 EndY=83.0051 EndZ=0
    g78: LineSegment [constr] StartX=17.5115 StartY=83.0051 StartZ=0 EndX=17.5115 EndY=98.0051 EndZ=0
    g79: LineSegment [constr] StartX=17.5115 StartY=57.9936 StartZ=0 EndX=17.5115 EndY=83.0051 EndZ=0
    g80: Circle CenterX=-7.5 CenterY=83.0051 CenterZ=0 NormalX=0 NormalY=0 NormalZ=1 AngleXU=0 Radius=1.7
    g81: Circle CenterX=-7.5 CenterY=98.0051 CenterZ=0 NormalX=0 NormalY=0 NormalZ=1 AngleXU=0 Radius=1.7
    g82: Circle CenterX=7.5 CenterY=98.0051 CenterZ=0 NormalX=0 NormalY=0 NormalZ=1 AngleXU=0 Radius=1.7
    g83: Circle CenterX=7.5 CenterY=83.0051 CenterZ=0 NormalX=0 NormalY=0 NormalZ=1 AngleXU=0 Radius=1.7
    g84: LineSegment [constr] StartX=-7.5 StartY=98.0051 StartZ=0 EndX=7.5 EndY=98.0051 EndZ=0
    g85: LineSegment [constr] StartX=7.5 StartY=98.0051 StartZ=0 EndX=7.5 EndY=83.0051 EndZ=0
    g86: LineSegment [constr] StartX=7.5 StartY=83.0051 StartZ=0 EndX=-7.5 EndY=83.0051 EndZ=0
    g87: LineSegment [constr] StartX=-7.5 StartY=83.0051 StartZ=0 EndX=-7.5 EndY=98.0051 EndZ=0
    g88: LineSegment [constr] StartX=17.5115 StartY=83.0051 StartZ=0 EndX=-7.5 EndY=83.0051 EndZ=0
    g89: Circle CenterX=-32.5115 CenterY=83.0051 CenterZ=0 NormalX=0 NormalY=0 NormalZ=1 AngleXU=0 Radius=1.7
    g90: Circle CenterX=-32.5115 CenterY=98.0051 CenterZ=0 NormalX=0 NormalY=0 NormalZ=1 AngleXU=0 Radius=1.7
    g91: Circle CenterX=-17.5115 CenterY=98.0051 CenterZ=0 NormalX=0 NormalY=0 NormalZ=1 AngleXU=0 Radius=1.7
    g92: Circle CenterX=-17.5115 CenterY=83.0051 CenterZ=0 NormalX=0 NormalY=0 NormalZ=1 AngleXU=0 Radius=1.7
    g93: LineSegment [constr] StartX=-32.5115 StartY=98.0051 StartZ=0 EndX=-17.5115 EndY=98.0051 EndZ=0
    g94: LineSegment [constr] StartX=-17.5115 StartY=98.0051 StartZ=0 EndX=-17.5115 EndY=83.0051 EndZ=0
    g95: LineSegment [constr] StartX=-17.5115 StartY=83.0051 StartZ=0 EndX=-32.5115 EndY=83.0051 EndZ=0
    g96: LineSegment [constr] StartX=-32.5115 StartY=83.0051 StartZ=0 EndX=-32.5115 EndY=98.0051 EndZ=0
    g97: LineSegment [constr] StartX=-7.5 StartY=83.0051 StartZ=0 EndX=-32.5115 EndY=83.0051 EndZ=0
    g98: Circle CenterX=-7.5 CenterY=90.5051 CenterZ=0 NormalX=0 NormalY=0 NormalZ=1 AngleXU=0 Radius=1.7
    g99: Circle CenterX=-7.5 CenterY=105.505 CenterZ=0 NormalX=0 NormalY=0 NormalZ=1 AngleXU=0 Radius=1.7
    g100: Circle CenterX=7.5 CenterY=105.505 CenterZ=0 NormalX=0 NormalY=0 NormalZ=1 AngleXU=0 Radius=1.7
    g101: Circle CenterX=7.5 CenterY=90.5051 CenterZ=0 NormalX=0 NormalY=0 NormalZ=1 AngleXU=0 Radius=1.7
    g102: LineSegment [constr] StartX=-7.5 StartY=105.505 StartZ=0 EndX=7.5 EndY=105.505 EndZ=0
    g103: LineSegment [constr] StartX=7.5 StartY=105.505 StartZ=0 EndX=7.5 EndY=90.5051 EndZ=0
    g104: LineSegment [constr] StartX=7.5 StartY=90.5051 StartZ=0 EndX=-7.5 EndY=90.5051 EndZ=0
    g105: LineSegment [constr] StartX=-7.5 StartY=90.5051 StartZ=0 EndX=-7.5 EndY=105.505 EndZ=0
    g106: LineSegment StartX=-30.5 StartY=0 StartZ=0 EndX=30.5 EndY=0 EndZ=0
    g107: Circle CenterX=-24.8274 CenterY=3 CenterZ=0 NormalX=0 NormalY=0 NormalZ=1 AngleXU=0 Radius=1.7
    g108: Circle CenterX=-7.5 CenterY=3 CenterZ=0 NormalX=0 NormalY=0 NormalZ=1 AngleXU=0 Radius=1.7
    g109: Circle CenterX=7.5 CenterY=3 CenterZ=0 NormalX=0 NormalY=0 NormalZ=1 AngleXU=0 Radius=1.7
    g110: Circle CenterX=25.1726 CenterY=3 CenterZ=0 NormalX=0 NormalY=0 NormalZ=1 AngleXU=0 Radius=1.7
    g111: LineSegment [constr] StartX=-24.8274 StartY=3 StartZ=0 EndX=-7.5 EndY=3 EndZ=0
    g112: LineSegment [constr] StartX=-7.5 StartY=3 StartZ=0 EndX=7.5 EndY=3 EndZ=0
    g113: LineSegment [constr] StartX=7.5 StartY=3 StartZ=0 EndX=25.1726 EndY=3 EndZ=0
  constraints (276):
    c: Horizontal(g0)
    c: Coincident(g0,g1)
    c: Vertical(g1)
    c: Coincident(g1,g2)
    c: Coincident(g2,g3)
    c: Vertical(g3)
    c: Coincident(g3,g4)
    c: Horizontal(g4)
    c: Coincident(g4,g5)
    c: Vertical(g5)
    c: Coincident(g8,g0)
    c: Vertical(g8)
    c: PointOnObject(g9,g-2)
    c: Tangent(g9,g6) = -1.5708
    c: Coincident(g10,g7)
    c: Coincident(g10,g6)
    c: Horizontal(g10)
    c: Tangent(g7,g11) = -1.5708
    c: Tangent(g8,g11) = -1.5708
    c: Tangent(g6,g12) = -1.5708
    c: Tangent(g5,g12) = -1.5708
    c: Equal(g12,g11)
    c: Coincident(g13,g8)
    c: Coincident(g13,g5)
    c: Horizontal(g13)
    c: Coincident(g14,g7)
    c: Coincident(g14,g6)
    c: Tangent(g7,g9) = -1.5708
    c: PointOnObject(g0,g-1)
    c: PointOnObject(g4,g-1)
    c: DistanceY(g-1,g2) = 6.5
    c: DistanceX(g1,g2) = 61
    c: Symmetric(g1,g2,g-2)
    c: DistanceX(g0,g4) = 105
    c: DistanceY(g2,g5) = 70
    c: Radius(g9) = 45
    c: Radius(g11) = 30
    c: Coincident(g8,g15)
    c: Vertical(g15)
    c: Coincident(g15,g16)
    c: Horizontal(g16)
    c: Tangent(g16,g9)
    c: Coincident(g16,g17)
    c: Coincident(g17,g5)
    c: Vertical(g17)
    c: DistanceY(g5,g16) = 45
    c: Coincident(g22,g23)
    c: Coincident(g23,g24)
    c: Coincident(g24,g25)
    c: Coincident(g25,g22)
    c: Horizontal(g22)
    c: Horizontal(g24)
    c: Vertical(g23)
    c: Vertical(g25)
    c: Coincident(g22,g19)
    c: Coincident(g23,g21)
    c: Equal(g20,g19)
    c: Equal(g19,g18)
    c: Equal(g18,g21)
    c: Radius(g19) = 1.7
    c: Coincident(g18,g24)
    c: Coincident(g20,g22)
    c: Equal(g22,g25)
    c: DistanceY(g25,g25) = 15
    c: Coincident(g30,g31)
    c: Coincident(g31,g32)
    c: Coincident(g32,g33)
    c: Coincident(g33,g30)
    c: Horizontal(g30)
    c: Horizontal(g32)
    c: Vertical(g31)
    c: Vertical(g33)
    c: Coincident(g30,g27)
    c: Coincident(g31,g29)
    c: Equal(g28,g27)
    c: Equal(g27,g26)
    c: Equal(g26,g29)
    c: Equal(g19,g27) = 1.7
    c: Coincident(g26,g32)
    c: Coincident(g28,g30)
    c: Equal(g30,g33)
    c: Equal(g25,g33) = 15
    c: Coincident(g18,g34)
    c: Coincident(g26,g34)
    c: Distance(g34) = 25.0115
    c: Angle(g34) = 3.14159
    c: Coincident(g39,g40)
    c: Coincident(g40,g41)
    c: Coincident(g41,g42)
    c: Coincident(g42,g39)
    c: Horizontal(g39)
    c: Horizontal(g41)
    c: Vertical(g40)
    c: Vertical(g42)
    c: Coincident(g39,g36)
    c: Coincident(g40,g38)
    c: Equal(g37,g36)
    c: Equal(g36,g35)
    c: Equal(g35,g38)
    c: Equal(g19,g36) = 1.7
    c: Coincident(g35,g41)
    c: Coincident(g37,g39)
    c: Equal(g39,g42)
    c: Equal(g25,g42) = 15
    c: Coincident(g26,g43)
    c: Coincident(g35,g43)
    c: Equal(g34,g43)
    c: Parallel(g43,g34)
    c: Coincident(g48,g49)
    c: Coincident(g49,g50)
    c: Coincident(g50,g51)
    c: Coincident(g51,g48)
    c: Horizontal(g48)
    c: Horizontal(g50)
    c: Vertical(g49)
    c: Vertical(g51)
    c: Coincident(g48,g45)
    c: Coincident(g49,g47)
    c: Equal(g46,g45)
    c: Equal(g45,g44)
    c: Equal(g44,g47)
    c: Equal(g19,g45) = 1.7
    c: Coincident(g44,g50)
    c: Coincident(g46,g48)
    c: Equal(g48,g51)
    c: Equal(g25,g51) = 15
    c: Coincident(g18,g52)
    c: Coincident(g44,g52)
    c: Equal(g52,g34)
    c: Perpendicular(g52,g34)
    c: Coincident(g57,g58)
    c: Coincident(g58,g59)
    c: Coincident(g59,g60)
    c: Coincident(g60,g57)
    c: Horizontal(g57)
    c: Horizontal(g59)
    c: Vertical(g58)
    c: Vertical(g60)
    c: Coincident(g57,g54)
    c: Coincident(g58,g56)
    c: Equal(g55,g54)
    c: Equal(g54,g53)
    c: Equal(g53,g56)
    c: Equal(g19,g54) = 1.7
    c: Coincident(g53,g59)
    c: Coincident(g55,g57)
    c: Equal(g57,g60)
    c: Equal(g25,g60) = 15
    c: Coincident(g44,g61)
    c: Coincident(g53,g61)
    c: Equal(g34,g61)
    c: Parallel(g61,g34)
    c: Coincident(g66,g67)
    c: Coincident(g67,g68)
    c: Coincident(g68,g69)
    c: Coincident(g69,g66)
    c: Horizontal(g66)
    c: Horizontal(g68)
    c: Vertical(g67)
    c: Vertical(g69)
    c: Coincident(g66,g63)
    c: Coincident(g67,g65)
    c: Equal(g64,g63)
    c: Equal(g63,g62)
    c: Equal(g62,g65)
    c: Equal(g19,g63) = 1.7
    c: Coincident(g62,g68)
    c: Coincident(g64,g66)
    c: Equal(g66,g69)
    c: Equal(g25,g69) = 15
    c: Coincident(g53,g70)
    c: Coincident(g62,g70)
    c: Equal(g34,g70)
    c: Parallel(g70,g34)
    c: Coincident(g75,g76)
    c: Coincident(g76,g77)
    c: Coincident(g77,g78)
    c: Coincident(g78,g75)
    c: Horizontal(g75)
    c: Horizontal(g77)
    c: Vertical(g76)
    c: Vertical(g78)
    c: Coincident(g75,g72)
    c: Coincident(g76,g74)
    c: Equal(g73,g72)
    c: Equal(g72,g71)
    c: Equal(g71,g74)
    c: Equal(g19,g72) = 1.7
    c: Coincident(g71,g77)
    c: Coincident(g73,g75)
    c: Equal(g75,g78)
    c: Equal(g25,g78) = 15
    c: Coincident(g44,g79)
    c: Coincident(g71,g79)
    c: Equal(g52,g79)
    c: Perpendicular(g79,g34)
    c: Coincident(g84,g85)
    c: Coincident(g85,g86)
    c: Coincident(g86,g87)
    c: Coincident(g87,g84)
    c: Horizontal(g86)
    c: Vertical(g85)
    c: Vertical(g87)
    c: Coincident(g84,g81)
    c: Coincident(g85,g83)
    c: Equal(g82,g81)
    c: Equal(g81,g80)
    c: Equal(g80,g83)
    c: Equal(g19,g81) = 1.7
    c: Coincident(g80,g86)
    c: Coincident(g82,g84)
    c: Equal(g84,g87)
    c: Equal(g25,g87) = 15
    c: Coincident(g71,g88)
    c: Coincident(g80,g88)
    c: Equal(g34,g88)
    c: Parallel(g88,g34)
    c: Coincident(g93,g94)
    c: Coincident(g94,g95)
    c: Coincident(g95,g96)
    c: Coincident(g96,g93)
    c: Horizontal(g93)
    c: Horizontal(g95)
    c: Vertical(g94)
    c: Vertical(g96)
    c: Coincident(g93,g90)
    c: Coincident(g94,g92)
    c: Equal(g91,g90)
    c: Equal(g90,g89)
    c: Equal(g89,g92)
    c: Equal(g19,g90) = 1.7
    c: Coincident(g89,g95)
    c: Coincident(g91,g93)
    c: Equal(g93,g96)
    c: Equal(g25,g96) = 15
    c: Coincident(g80,g97)
    c: Coincident(g89,g97)
    c: Equal(g34,g97)
    c: Parallel(g97,g34)
    c: Symmetric(g82,g81,g-2)
    c: Coincident(g102,g103)
    c: Coincident(g103,g104)
    c: Coincident(g104,g105)
    c: Coincident(g105,g102)
    c: Horizontal(g104)
    c: Vertical(g105)
    c: Coincident(g102,g99)
    c: Coincident(g103,g101)
    c: Equal(g100,g99)
    c: Equal(g99,g98)
    c: Equal(g98,g101)
    c: Coincident(g98,g104)
    c: Coincident(g100,g102)
    c: Equal(g102,g105)
    c: Equal(g101,g81)
    c: Equal(g102,g93)
    c: Symmetric(g99,g100,g-2)
    c: Symmetric(g101,g100,g82)
    c: Coincident(g106,g0)
    c: Coincident(g106,g4)
    c: Coincident(g111,g107)
    c: Coincident(g111,g108)
    c: Horizontal(g111)
    c: Coincident(g112,g109)
    c: Coincident(g113,g109)
    c: Coincident(g113,g110)
    c: Horizontal(g113)
    c: Equal(g110,g109)
    c: Equal(g109,g108)
    c: Equal(g108,g107)
    c: Radius(g107) = 1.7
    c: Coincident(g108,g112)
    c: DistanceX(g107,g110) = 50
    c: Symmetric(g108,g109,g-2)
    c: DistanceX(g108,g109) = 15
    c: DistanceY(g0,g107) = 3
FEATURE [PartDesign::Pad] Pad004  label="TimonePortaBatterie001"
  Length = 2
  Length2 = 100
  Profile = -> Sketch023
  Type = 0
FEATURE [Sketcher::SketchObject] Sketch024  label="TimonePortaBatterie003"
  MapMode = 5
  Placement = pos=(0,0,2) rot=(0,0,1;0rad)
  Support = -> [Pad004]
  sketch-geometry (48):
    g0: LineSegment StartX=-52.5 StartY=0 StartZ=0 EndX=-30.5 EndY=0 EndZ=0
    g1: LineSegment StartX=-30.5 StartY=0 StartZ=0 EndX=-30.5 EndY=6.5 EndZ=0
    g2: LineSegment StartX=-30.5 StartY=6.5 StartZ=0 EndX=30.5 EndY=6.5 EndZ=0
    g3: LineSegment StartX=30.5 StartY=6.5 StartZ=0 EndX=30.5 EndY=0 EndZ=0
    g4: LineSegment StartX=30.5 StartY=0 StartZ=0 EndX=52.5 EndY=0 EndZ=0
    g5: LineSegment StartX=52.5 StartY=0 StartZ=0 EndX=52.5 EndY=76.5 EndZ=0
    g6: LineSegment StartX=42.5 StartY=98.8607 StartZ=0 EndX=30 EndY=110.041 EndZ=0
    g7: LineSegment StartX=-30 StartY=110.041 StartZ=0 EndX=-42.5 EndY=98.8607 EndZ=0
    g8: LineSegment StartX=-52.5 StartY=76.5 StartZ=0 EndX=-52.5 EndY=0 EndZ=0
    g9: ArcOfCircle CenterX=0 CenterY=76.5 CenterZ=0 NormalX=0 NormalY=0 NormalZ=1 AngleXU=0 Radius=45 StartAngle=0.841069 EndAngle=2.30052
    g10: LineSegment [constr] StartX=-30 StartY=110.041 StartZ=0 EndX=30 EndY=110.041 EndZ=0
    g11: ArcOfCircle CenterX=-22.5 CenterY=76.5 CenterZ=0 NormalX=0 NormalY=0 NormalZ=1 AngleXU=0 Radius=30 StartAngle=2.30052 EndAngle=3.14159
    g12: ArcOfCircle CenterX=22.5 CenterY=76.5 CenterZ=0 NormalX=0 NormalY=0 NormalZ=1 AngleXU=0 Radius=30 StartAngle=1e-16 EndAngle=0.841069
    g13: LineSegment [constr] StartX=-52.5 StartY=76.5 StartZ=0 EndX=52.5 EndY=76.5 EndZ=0
    g14: LineSegment [constr] StartX=-42.5 StartY=98.8607 StartZ=0 EndX=42.5 EndY=98.8607 EndZ=0
    g15: LineSegment [constr] StartX=-52.5 StartY=76.5 StartZ=0 EndX=-52.5 EndY=121.5 EndZ=0
    g16: LineSegment [constr] StartX=-52.5 StartY=121.5 StartZ=0 EndX=52.5 EndY=121.5 EndZ=0
    g17: LineSegment [constr] StartX=52.5 StartY=121.5 StartZ=0 EndX=52.5 EndY=76.5 EndZ=0
    g18: LineSegment [constr] StartX=-30.5 StartY=0 StartZ=0 EndX=30.5 EndY=0 EndZ=0
    g19: Circle [constr] CenterX=-24.8274 CenterY=3 CenterZ=0 NormalX=0 NormalY=0 NormalZ=1 AngleXU=0 Radius=1.7
    g20: Circle [constr] CenterX=-7.5 CenterY=3 CenterZ=0 NormalX=0 NormalY=0 NormalZ=1 AngleXU=0 Radius=1.7
    g21: Circle [constr] CenterX=7.5 CenterY=3 CenterZ=0 NormalX=0 NormalY=0 NormalZ=1 AngleXU=0 Radius=1.7
    g22: Circle [constr] CenterX=25.1726 CenterY=3 CenterZ=0 NormalX=0 NormalY=0 NormalZ=1 AngleXU=0 Radius=1.7
    g23: LineSegment [constr] StartX=-24.8274 StartY=3 StartZ=0 EndX=-7.5 EndY=3 EndZ=0
    g24: LineSegment [constr] StartX=-7.5 StartY=3 StartZ=0 EndX=7.5 EndY=3 EndZ=0
    g25: LineSegment [constr] StartX=7.5 StartY=3 StartZ=0 EndX=25.1726 EndY=3 EndZ=0
    g26: LineSegment StartX=-50.5 StartY=2 StartZ=0 EndX=-50.5 EndY=76.5 EndZ=0
    g27: LineSegment StartX=-40.1262 StartY=98.8607 StartZ=0 EndX=-26.9073 EndY=110.041 EndZ=0
    g28: LineSegment StartX=26.9073 StartY=110.041 StartZ=0 EndX=40.1262 EndY=98.8607 EndZ=0
    g29: LineSegment StartX=50.5 StartY=76.5 StartZ=0 EndX=50.5 EndY=2.77908 EndZ=0
    g30: LineSegment StartX=50.5 StartY=2.77908 StartZ=0 EndX=35.5 EndY=2.77908 EndZ=0
    g31: LineSegment StartX=32.5 StartY=5.77908 StartZ=0 EndX=32.5 EndY=9.5 EndZ=0
    g32: LineSegment StartX=32.5 StartY=9.5 StartZ=0 EndX=-32.5 EndY=9.5 EndZ=0
    g33: LineSegment StartX=-32.5 StartY=9.5 StartZ=0 EndX=-32.5 EndY=5 EndZ=0
    g34: LineSegment StartX=-35.5 StartY=2 StartZ=0 EndX=-50.5 EndY=2 EndZ=0
    g35: ArcOfCircle CenterX=-21.2139 CenterY=76.5 CenterZ=0 NormalX=0 NormalY=0 NormalZ=1 AngleXU=0 Radius=29.2861 StartAngle=2.27284 EndAngle=3.14159
    g36: ArcOfCircle CenterX=21.2139 CenterY=76.5 CenterZ=0 NormalX=0 NormalY=0 NormalZ=1 AngleXU=0 Radius=29.2861 StartAngle=0 EndAngle=0.868755
    g37: ArcOfCircle CenterX=0 CenterY=76.5 CenterZ=0 NormalX=0 NormalY=0 NormalZ=1 AngleXU=0 Radius=43 StartAngle=0.894703 EndAngle=2.24689
    g38: LineSegment [constr] StartX=-50.5 StartY=2 StartZ=0 EndX=-50.5 EndY=0 EndZ=0
    g39: LineSegment [constr] StartX=-30.5 StartY=6.5 StartZ=0 EndX=-32.5 EndY=6.5 EndZ=0
    g40: LineSegment [constr] StartX=32.5 StartY=2.77908 StartZ=0 EndX=30.5 EndY=2.77908 EndZ=0
    g41: LineSegment [constr] StartX=50.5 StartY=2.77908 StartZ=0 EndX=52.5 EndY=2.77908 EndZ=0
    g42: LineSegment [constr] StartX=0.211269 StartY=121.5 StartZ=0 EndX=0.211269 EndY=119.5 EndZ=0
    g43: LineSegment [constr] StartX=-30.5 StartY=6.5 StartZ=0 EndX=-30.5 EndY=9.5 EndZ=0
    g44: ArcOfCircle CenterX=-35.5 CenterY=5 CenterZ=0 NormalX=0 NormalY=0 NormalZ=1 AngleXU=0 Radius=3 StartAngle=4.71239 EndAngle=6.28319
    g45: ArcOfCircle CenterX=35.5 CenterY=5.77908 CenterZ=0 NormalX=0 NormalY=0 NormalZ=1 AngleXU=0 Radius=3 StartAngle=3.14159 EndAngle=4.71239
    g46: LineSegment [constr] StartX=32.5 StartY=5.77908 StartZ=0 EndX=32.5 EndY=2.77908 EndZ=0
    g47: LineSegment [constr] StartX=32.5 StartY=2.77908 StartZ=0 EndX=35.5 EndY=2.77908 EndZ=0
  constraints (124):
    c: Horizontal(g0)
    c: Coincident(g0,g1)
    c: Vertical(g1)
    c: Coincident(g1,g2)
    c: Coincident(g2,g3)
    c: Vertical(g3)
    c: Coincident(g3,g4)
    c: Horizontal(g4)
    c: Coincident(g4,g5)
    c: Vertical(g5)
    c: Coincident(g8,g0)
    c: Vertical(g8)
    c: PointOnObject(g9,g-2)
    c: Tangent(g9,g6) = -1.5708
    c: Coincident(g10,g7)
    c: Coincident(g10,g6)
    c: Horizontal(g10)
    c: Tangent(g7,g11) = -1.5708
    c: Tangent(g8,g11) = -1.5708
    c: Tangent(g6,g12) = -1.5708
    c: Tangent(g5,g12) = -1.5708
    c: Equal(g12,g11)
    c: Coincident(g13,g8)
    c: Coincident(g13,g5)
    c: Horizontal(g13)
    c: Coincident(g14,g7)
    c: Coincident(g14,g6)
    c: Tangent(g7,g9) = -1.5708
    c: PointOnObject(g0,g-1)
    c: PointOnObject(g4,g-1)
    c: DistanceY(g-1,g2) = 6.5
    c: DistanceX(g1,g2) = 61
    c: Symmetric(g1,g2,g-2)
    c: DistanceX(g0,g4) = 105
    c: DistanceY(g2,g5) = 70
    c: Radius(g9) = 45
    c: Radius(g11) = 30
    c: Coincident(g8,g15)
    c: Vertical(g15)
    c: Coincident(g15,g16)
    c: Horizontal(g16)
    c: Tangent(g16,g9)
    c: Coincident(g16,g17)
    c: Coincident(g17,g5)
    c: Vertical(g17)
    c: DistanceY(g5,g16) = 45
    c: Coincident(g18,g0)
    c: Coincident(g18,g4)
    c: Coincident(g23,g19)
    c: Coincident(g23,g20)
    c: Horizontal(g23)
    c: Coincident(g24,g21)
    c: Coincident(g25,g21)
    c: Coincident(g25,g22)
    c: Horizontal(g25)
    c: Equal(g22,g21)
    c: Equal(g21,g20)
    c: Equal(g20,g19)
    c: Radius(g19) = 1.7
    c: Coincident(g20,g24)
    c: DistanceX(g19,g22) = 50
    c: Symmetric(g20,g21,g-2)
    c: DistanceX(g20,g21) = 15
    c: DistanceY(g0,g19) = 3
    c: Vertical(g26)
    c: Vertical(g29)
    c: Coincident(g29,g30)
    c: Coincident(g31,g32)
    c: Coincident(g32,g33)
    c: Coincident(g34,g26)
    c: Tangent(g26,g35) = 1.5708
    c: Tangent(g27,g35) = 1.5708
    c: Tangent(g28,g36) = 1.5708
    c: Tangent(g29,g36) = 1.5708
    c: Coincident(g37,g9)
    c: Coincident(g37,g27)
    c: PointOnObject(g27,g10)
    c: Coincident(g37,g28)
    c: PointOnObject(g28,g10)
    c: PointOnObject(g26,g13)
    c: PointOnObject(g29,g13)
    c: Horizontal(g32)
    c: Vertical(g33)
    c: Horizontal(g34)
    c: Horizontal(g30)
    c: Vertical(g31)
    c: DistanceX(g0,g26) = 2
    c: DistanceY(g0,g26) = 2
    c: Coincident(g38,g26)
    c: PointOnObject(g38,g0)
    c: Vertical(g38)
    c: Coincident(g39,g1)
    c: PointOnObject(g39,g33)
    c: Horizontal(g39)
    c: Equal(g39,g38)
    c: PointOnObject(g40,g3)
    c: Horizontal(g40)
    c: Coincident(g41,g29)
    c: PointOnObject(g41,g5)
    c: Horizontal(g41)
    c: Equal(g41,g40)
    c: Equal(g40,g38)
    c: PointOnObject(g27,g14)
    c: PointOnObject(g28,g14)
    c: PointOnObject(g42,g9)
    c: PointOnObject(g42,g37)
    c: Vertical(g42)
    c: DistanceY(g42,g42) = 2
    c: Coincident(g43,g1)
    c: PointOnObject(g43,g32)
    c: Vertical(g43)
    c: DistanceY(g43,g43) = 3
    c: Tangent(g34,g44) = 1.5708
    c: Tangent(g33,g44) = 1.5708
    c: Radius(g44) = 3
    c: Tangent(g31,g45) = 1.5708
    c: Tangent(g30,g45) = 1.5708
    c: Coincident(g46,g31)
    c: Coincident(g46,g40)
    c: Coincident(g47,g40)
    c: Coincident(g47,g30)
    c: Radius(g45) = 3
    c: Horizontal(g47)
    c: Vertical(g46)
FEATURE [PartDesign::Pad] Pad005  label="Timone Porta Batterie001"
  BaseFeature = -> Pad004
  Length = 2
  Length2 = 100
  Profile = -> Sketch024
  Type = 0
FEATURE [Sketcher::SketchObject] Sketch025  label="TimonePortaBatterie004"
  MapMode = 5
  Placement = pos=(0,0,4) rot=(0,0,1;0rad)
  Support = -> [Pad005]
  sketch-geometry (60):
    g0: LineSegment StartX=-52.5 StartY=0 StartZ=0 EndX=-30.5 EndY=0 EndZ=0
    g1: LineSegment StartX=-30.5 StartY=0 StartZ=0 EndX=-30.5 EndY=6.5 EndZ=0
    g2: LineSegment StartX=-20 StartY=6.5 StartZ=0 EndX=20 EndY=6.5 EndZ=0
    g3: LineSegment StartX=30.5 StartY=6.5 StartZ=0 EndX=30.5 EndY=0 EndZ=0
    g4: LineSegment StartX=30.5 StartY=0 StartZ=0 EndX=52.5 EndY=0 EndZ=0
    g5: LineSegment [constr] StartX=52.5 StartY=0 StartZ=0 EndX=52.5 EndY=76.5 EndZ=0
    g6: LineSegment [constr] StartX=42.5 StartY=98.8607 StartZ=0 EndX=30 EndY=110.041 EndZ=0
    g7: LineSegment [constr] StartX=-30 StartY=110.041 StartZ=0 EndX=-42.5 EndY=98.8607 EndZ=0
    g8: LineSegment [constr] StartX=-52.5 StartY=76.5 StartZ=0 EndX=-52.5 EndY=0 EndZ=0
    g9: ArcOfCircle [constr] CenterX=0 CenterY=76.5 CenterZ=0 NormalX=0 NormalY=0 NormalZ=1 AngleXU=0 Radius=45 StartAngle=0.841069 EndAngle=2.30052
    g10: LineSegment [constr] StartX=-30 StartY=110.041 StartZ=0 EndX=30 EndY=110.041 EndZ=0
    g11: ArcOfCircle [constr] CenterX=-22.5 CenterY=76.5 CenterZ=0 NormalX=0 NormalY=0 NormalZ=1 AngleXU=0 Radius=30 StartAngle=2.30052 EndAngle=3.14159
    g12: ArcOfCircle [constr] CenterX=22.5 CenterY=76.5 CenterZ=0 NormalX=0 NormalY=0 NormalZ=1 AngleXU=0 Radius=30 StartAngle=1e-16 EndAngle=0.841069
    g13: LineSegment [constr] StartX=-52.5 StartY=76.5 StartZ=0 EndX=52.5 EndY=76.5 EndZ=0
    g14: LineSegment [constr] StartX=-42.5 StartY=98.8607 StartZ=0 EndX=42.5 EndY=98.8607 EndZ=0
    g15: LineSegment [constr] StartX=-52.5 StartY=76.5 StartZ=0 EndX=-52.5 EndY=121.5 EndZ=0
    g16: LineSegment [constr] StartX=-52.5 StartY=121.5 StartZ=0 EndX=52.5 EndY=121.5 EndZ=0
    g17: LineSegment [constr] StartX=52.5 StartY=121.5 StartZ=0 EndX=52.5 EndY=76.5 EndZ=0
    g18: LineSegment [constr] StartX=-30.5 StartY=0 StartZ=0 EndX=30.5 EndY=0 EndZ=0
    g19: Circle [constr] CenterX=-24.8274 CenterY=3 CenterZ=0 NormalX=0 NormalY=0 NormalZ=1 AngleXU=0 Radius=1.7
    g20: Circle [constr] CenterX=-7.5 CenterY=3 CenterZ=0 NormalX=0 NormalY=0 NormalZ=1 AngleXU=0 Radius=1.7
    g21: Circle [constr] CenterX=7.5 CenterY=3 CenterZ=0 NormalX=0 NormalY=0 NormalZ=1 AngleXU=0 Radius=1.7
    g22: Circle [constr] CenterX=25.1726 CenterY=3 CenterZ=0 NormalX=0 NormalY=0 NormalZ=1 AngleXU=0 Radius=1.7
    g23: LineSegment [constr] StartX=-24.8274 StartY=3 StartZ=0 EndX=-7.5 EndY=3 EndZ=0
    g24: LineSegment [constr] StartX=-7.5 StartY=3 StartZ=0 EndX=7.5 EndY=3 EndZ=0
    g25: LineSegment [constr] StartX=7.5 StartY=3 StartZ=0 EndX=25.1726 EndY=3 EndZ=0
    g26: LineSegment [constr] StartX=-50.5 StartY=2 StartZ=0 EndX=-50.5 EndY=76.5 EndZ=0
    g27: LineSegment [constr] StartX=-40.1262 StartY=98.8607 StartZ=0 EndX=-26.9073 EndY=110.041 EndZ=0
    g28: LineSegment [constr] StartX=26.9073 StartY=110.041 StartZ=0 EndX=40.1262 EndY=98.8607 EndZ=0
    g29: LineSegment [constr] StartX=50.5 StartY=76.5 StartZ=0 EndX=50.5 EndY=2.77908 EndZ=0
    g30: LineSegment StartX=50.5 StartY=2.77908 StartZ=0 EndX=35.5 EndY=2.77908 EndZ=0
    g31: LineSegment StartX=32.5 StartY=5.77908 StartZ=0 EndX=32.5 EndY=9.5 EndZ=0
    g32: LineSegment StartX=20 StartY=9.5 StartZ=0 EndX=-20 EndY=9.5 EndZ=0
    g33: LineSegment StartX=-32.5 StartY=9.5 StartZ=0 EndX=-32.5 EndY=5 EndZ=0
    g34: LineSegment StartX=-35.5 StartY=2 StartZ=0 EndX=-50.5 EndY=2 EndZ=0
    g35: ArcOfCircle [constr] CenterX=-21.2139 CenterY=76.5 CenterZ=0 NormalX=0 NormalY=0 NormalZ=1 AngleXU=0 Radius=29.2861 StartAngle=2.27284 EndAngle=3.14159
    g36: ArcOfCircle [constr] CenterX=21.2139 CenterY=76.5 CenterZ=0 NormalX=0 NormalY=0 NormalZ=1 AngleXU=0 Radius=29.2861 StartAngle=0 EndAngle=0.868755
    g37: ArcOfCircle [constr] CenterX=0 CenterY=76.5 CenterZ=0 NormalX=0 NormalY=0 NormalZ=1 AngleXU=0 Radius=43 StartAngle=0.894703 EndAngle=2.24689
    g38: LineSegment [constr] StartX=-50.5 StartY=2 StartZ=0 EndX=-50.5 EndY=0 EndZ=0
    g39: LineSegment [constr] StartX=-30.5 StartY=6.5 StartZ=0 EndX=-32.5 EndY=6.5 EndZ=0
    g40: LineSegment [constr] StartX=32.5 StartY=2.77908 StartZ=0 EndX=30.5 EndY=2.77908 EndZ=0
    g41: LineSegment StartX=50.5 StartY=2.77908 StartZ=0 EndX=52.5 EndY=2.77908 EndZ=0
    g42: LineSegment [constr] StartX=0.211269 StartY=121.5 StartZ=0 EndX=0.211269 EndY=119.5 EndZ=0
    g43: LineSegment [constr] StartX=-30.5 StartY=6.5 StartZ=0 EndX=-30.5 EndY=9.5 EndZ=0
    g44: ArcOfCircle CenterX=-35.5 CenterY=5 CenterZ=0 NormalX=0 NormalY=0 NormalZ=1 AngleXU=0 Radius=3 StartAngle=4.71239 EndAngle=6.28319
    g45: ArcOfCircle CenterX=35.5 CenterY=5.77908 CenterZ=0 NormalX=0 NormalY=0 NormalZ=1 AngleXU=0 Radius=3 StartAngle=3.14159 EndAngle=4.71239
    g46: LineSegment [constr] StartX=32.5 StartY=5.77908 StartZ=0 EndX=32.5 EndY=2.77908 EndZ=0
    g47: LineSegment [constr] StartX=32.5 StartY=2.77908 StartZ=0 EndX=35.5 EndY=2.77908 EndZ=0
    g48: LineSegment StartX=52.5 StartY=2.77908 StartZ=0 EndX=52.5 EndY=0 EndZ=0
    g49: LineSegment StartX=30.5 StartY=6.5 StartZ=0 EndX=32.5 EndY=9.5 EndZ=0
    g50: LineSegment StartX=-32.5 StartY=9.5 StartZ=0 EndX=-30.5 EndY=6.5 EndZ=0
    g51: LineSegment StartX=-20 StartY=9.5 StartZ=0 EndX=-20 EndY=6.5 EndZ=0
    g52: LineSegment StartX=20 StartY=9.5 StartZ=0 EndX=20 EndY=6.5 EndZ=0
    g53: LineSegment [constr] StartX=-30.5 StartY=9.5 StartZ=0 EndX=-32.5 EndY=9.5 EndZ=0
    g54: LineSegment [constr] StartX=-30.5 StartY=9.5 StartZ=0 EndX=-20 EndY=9.5 EndZ=0
    g55: LineSegment [constr] StartX=-30.5 StartY=6.5 StartZ=0 EndX=-20 EndY=6.5 EndZ=0
    g56: LineSegment [constr] StartX=20 StartY=9.5 StartZ=0 EndX=32.5 EndY=9.5 EndZ=0
    g57: LineSegment [constr] StartX=20 StartY=6.5 StartZ=0 EndX=30.5 EndY=6.5 EndZ=0
    g58: LineSegment StartX=-50.5 StartY=2 StartZ=0 EndX=-52.5 EndY=2 EndZ=0
    g59: LineSegment StartX=-52.5 StartY=2 StartZ=0 EndX=-52.5 EndY=0 EndZ=0
  constraints (149):
    c: Horizontal(g0)
    c: Coincident(g0,g1)
    c: Vertical(g1)
    c: Vertical(g3)
    c: Coincident(g3,g4)
    c: Horizontal(g4)
    c: Coincident(g4,g5)
    c: Vertical(g5)
    c: Coincident(g8,g0)
    c: Vertical(g8)
    c: PointOnObject(g9,g-2)
    c: Tangent(g9,g6) = -1.5708
    c: Coincident(g10,g7)
    c: Coincident(g10,g6)
    c: Horizontal(g10)
    c: Tangent(g7,g11) = -1.5708
    c: Tangent(g8,g11) = -1.5708
    c: Tangent(g6,g12) = -1.5708
    c: Tangent(g5,g12) = -1.5708
    c: Equal(g12,g11)
    c: Coincident(g13,g8)
    c: Coincident(g13,g5)
    c: Horizontal(g13)
    c: Coincident(g14,g7)
    c: Coincident(g14,g6)
    c: Tangent(g7,g9) = -1.5708
    c: PointOnObject(g0,g-1)
    c: PointOnObject(g4,g-1)
    c: DistanceY(g-1,g3) = 6.5
    c: DistanceX(g1,g3) = 61
    c: DistanceX(g0,g4) = 105
    c: DistanceY(g3,g5) = 70
    c: Radius(g9) = 45
    c: Radius(g11) = 30
    c: Coincident(g8,g15)
    c: Vertical(g15)
    c: Coincident(g15,g16)
    c: Horizontal(g16)
    c: Tangent(g16,g9)
    c: Coincident(g16,g17)
    c: Coincident(g17,g5)
    c: Vertical(g17)
    c: DistanceY(g5,g16) = 45
    c: Coincident(g18,g0)
    c: Coincident(g18,g4)
    c: Coincident(g23,g19)
    c: Coincident(g23,g20)
    c: Horizontal(g23)
    c: Coincident(g24,g21)
    c: Coincident(g25,g21)
    c: Coincident(g25,g22)
    c: Horizontal(g25)
    c: Equal(g22,g21)
    c: Equal(g21,g20)
    c: Equal(g20,g19)
    c: Radius(g19) = 1.7
    c: Coincident(g20,g24)
    c: DistanceX(g19,g22) = 50
    c: Symmetric(g20,g21,g-2)
    c: DistanceX(g20,g21) = 15
    c: DistanceY(g0,g19) = 3
    c: Vertical(g26)
    c: Vertical(g29)
    c: Coincident(g29,g30)
    c: Coincident(g53,g33)
    c: Coincident(g34,g26)
    c: Tangent(g26,g35) = 1.5708
    c: Tangent(g27,g35) = 1.5708
    c: Tangent(g28,g36) = 1.5708
    c: Tangent(g29,g36) = 1.5708
    c: Coincident(g37,g9)
    c: Coincident(g37,g27)
    c: PointOnObject(g27,g10)
    c: Coincident(g37,g28)
    c: PointOnObject(g28,g10)
    c: PointOnObject(g26,g13)
    c: PointOnObject(g29,g13)
    c: Horizontal(g32)
    c: Vertical(g33)
    c: Horizontal(g34)
    c: Horizontal(g30)
    c: Vertical(g31)
    c: DistanceX(g0,g26) = 2
    c: DistanceY(g0,g26) = 2
    c: Coincident(g38,g26)
    c: PointOnObject(g38,g0)
    c: Vertical(g38)
    c: Coincident(g39,g1)
    c: PointOnObject(g39,g33)
    c: Horizontal(g39)
    c: Equal(g39,g38)
    c: PointOnObject(g40,g3)
    c: Horizontal(g40)
    c: Coincident(g41,g29)
    c: PointOnObject(g41,g5)
    c: Horizontal(g41)
    c: Equal(g41,g40)
    c: Equal(g40,g38)
    c: PointOnObject(g27,g14)
    c: PointOnObject(g28,g14)
    c: PointOnObject(g42,g9)
    c: PointOnObject(g42,g37)
    c: Vertical(g42)
    c: DistanceY(g42,g42) = 2
    c: Coincident(g43,g1)
    c: Vertical(g43)
    c: Tangent(g34,g44) = 1.5708
    c: Tangent(g33,g44) = 1.5708
    c: Radius(g44) = 3
    c: Tangent(g31,g45) = 1.5708
    c: Tangent(g30,g45) = 1.5708
    c: Coincident(g46,g31)
    c: Coincident(g46,g40)
    c: Coincident(g47,g40)
    c: Coincident(g47,g30)
    c: Radius(g45) = 3
    c: Horizontal(g47)
    c: Vertical(g46)
    c: Coincident(g48,g41)
    c: Coincident(g48,g4)
    c: Coincident(g49,g3)
    c: Coincident(g49,g31)
    c: Equal(g40,g39)
    c: Coincident(g50,g53)
    c: Coincident(g50,g1)
    c: Vertical(g51)
    c: Vertical(g52)
    c: PointOnObject(g32,g51)
    c: Coincident(g53,g43)
    c: Tangent(g32,g53)
    c: Coincident(g2,g51)
    c: Coincident(g54,g53)
    c: Coincident(g54,g32)
    c: Coincident(g55,g1)
    c: Coincident(g55,g2)
    c: Horizontal(g55)
    c: Coincident(g2,g52)
    c: Coincident(g32,g52)
    c: Coincident(g56,g32)
    c: Coincident(g56,g31)
    c: Horizontal(g56)
    c: Coincident(g57,g2)
    c: Coincident(g57,g3)
    c: Horizontal(g57)
    c: Coincident(g58,g34)
    c: PointOnObject(g58,g8)
    c: Horizontal(g58)
    c: Coincident(g59,g58)
    c: Coincident(g59,g0)
FEATURE [PartDesign::Pad] Pad006  label="Timone Porta Batterie002"
  BaseFeature = -> Pad005
  Length = 25
  Length2 = 100
  Profile = -> Sketch025
  Type = 0
FEATURE [Sketcher::SketchObject] Sketch026  label="TimonePortaBatterie005"
  MapMode = 5
  Placement = pos=(0,0,29) rot=(0,0,1;0rad)
  Support = -> [Pad006]
  sketch-geometry (51):
    g0: LineSegment StartX=-52.5 StartY=0 StartZ=0 EndX=-30.5 EndY=0 EndZ=0
    g1: LineSegment StartX=-30.5 StartY=0 StartZ=0 EndX=-30.5 EndY=6.5 EndZ=0
    g2: LineSegment StartX=-30.5 StartY=6.5 StartZ=0 EndX=30.5 EndY=6.5 EndZ=0
    g3: LineSegment StartX=30.5 StartY=6.5 StartZ=0 EndX=30.5 EndY=0 EndZ=0
    g4: LineSegment StartX=30.5 StartY=0 StartZ=0 EndX=52.5 EndY=0 EndZ=0
    g5: LineSegment [constr] StartX=52.5 StartY=0 StartZ=0 EndX=52.5 EndY=76.5 EndZ=0
    g6: LineSegment [constr] StartX=42.5 StartY=98.8607 StartZ=0 EndX=30 EndY=110.041 EndZ=0
    g7: LineSegment [constr] StartX=-30 StartY=110.041 StartZ=0 EndX=-42.5 EndY=98.8607 EndZ=0
    g8: LineSegment [constr] StartX=-52.5 StartY=76.5 StartZ=0 EndX=-52.5 EndY=0 EndZ=0
    g9: ArcOfCircle [constr] CenterX=0 CenterY=76.5 CenterZ=0 NormalX=0 NormalY=0 NormalZ=1 AngleXU=0 Radius=45 StartAngle=0.841069 EndAngle=2.30052
    g10: LineSegment [constr] StartX=-30 StartY=110.041 StartZ=0 EndX=30 EndY=110.041 EndZ=0
    g11: ArcOfCircle [constr] CenterX=-22.5 CenterY=76.5 CenterZ=0 NormalX=0 NormalY=0 NormalZ=1 AngleXU=0 Radius=30 StartAngle=2.30052 EndAngle=3.14159
    g12: ArcOfCircle [constr] CenterX=22.5 CenterY=76.5 CenterZ=0 NormalX=0 NormalY=0 NormalZ=1 AngleXU=0 Radius=30 StartAngle=1e-16 EndAngle=0.841069
    g13: LineSegment [constr] StartX=-52.5 StartY=76.5 StartZ=0 EndX=52.5 EndY=76.5 EndZ=0
    g14: LineSegment [constr] StartX=-42.5 StartY=98.8607 StartZ=0 EndX=42.5 EndY=98.8607 EndZ=0
    g15: LineSegment [constr] StartX=-52.5 StartY=76.5 StartZ=0 EndX=-52.5 EndY=121.5 EndZ=0
    g16: LineSegment [constr] StartX=-52.5 StartY=121.5 StartZ=0 EndX=52.5 EndY=121.5 EndZ=0
    g17: LineSegment [constr] StartX=52.5 StartY=121.5 StartZ=0 EndX=52.5 EndY=76.5 EndZ=0
    g18: LineSegment [constr] StartX=-30.5 StartY=0 StartZ=0 EndX=30.5 EndY=0 EndZ=0
    g19: Circle [constr] CenterX=-24.8274 CenterY=3 CenterZ=0 NormalX=0 NormalY=0 NormalZ=1 AngleXU=0 Radius=1.7
    g20: Circle [constr] CenterX=-7.5 CenterY=3 CenterZ=0 NormalX=0 NormalY=0 NormalZ=1 AngleXU=0 Radius=1.7
    g21: Circle [constr] CenterX=7.5 CenterY=3 CenterZ=0 NormalX=0 NormalY=0 NormalZ=1 AngleXU=0 Radius=1.7
    g22: Circle [constr] CenterX=25.1726 CenterY=3 CenterZ=0 NormalX=0 NormalY=0 NormalZ=1 AngleXU=0 Radius=1.7
    g23: LineSegment [constr] StartX=-24.8274 StartY=3 StartZ=0 EndX=-7.5 EndY=3 EndZ=0
    g24: LineSegment [constr] StartX=-7.5 StartY=3 StartZ=0 EndX=7.5 EndY=3 EndZ=0
    g25: LineSegment [constr] StartX=7.5 StartY=3 StartZ=0 EndX=25.1726 EndY=3 EndZ=0
    g26: LineSegment [constr] StartX=-50.5 StartY=2 StartZ=0 EndX=-50.5 EndY=76.5 EndZ=0
    g27: LineSegment [constr] StartX=-40.1262 StartY=98.8607 StartZ=0 EndX=-26.9073 EndY=110.041 EndZ=0
    g28: LineSegment [constr] StartX=26.9073 StartY=110.041 StartZ=0 EndX=40.1262 EndY=98.8607 EndZ=0
    g29: LineSegment [constr] StartX=50.5 StartY=76.5 StartZ=0 EndX=50.5 EndY=2.77908 EndZ=0
    g30: LineSegment StartX=50.5 StartY=2.77908 StartZ=0 EndX=35.5 EndY=2.77908 EndZ=0
    g31: LineSegment StartX=32.5 StartY=5.77908 StartZ=0 EndX=32.5 EndY=9.5 EndZ=0
    g32: LineSegment StartX=32.5 StartY=9.5 StartZ=0 EndX=-32.5 EndY=9.5 EndZ=0
    g33: LineSegment StartX=-32.5 StartY=9.5 StartZ=0 EndX=-32.5 EndY=5 EndZ=0
    g34: LineSegment StartX=-35.5 StartY=2 StartZ=0 EndX=-50.5 EndY=2 EndZ=0
    g35: ArcOfCircle [constr] CenterX=-21.2139 CenterY=76.5 CenterZ=0 NormalX=0 NormalY=0 NormalZ=1 AngleXU=0 Radius=29.2861 StartAngle=2.27284 EndAngle=3.14159
    g36: ArcOfCircle [constr] CenterX=21.2139 CenterY=76.5 CenterZ=0 NormalX=0 NormalY=0 NormalZ=1 AngleXU=0 Radius=29.2861 StartAngle=0 EndAngle=0.868755
    g37: ArcOfCircle [constr] CenterX=0 CenterY=76.5 CenterZ=0 NormalX=0 NormalY=0 NormalZ=1 AngleXU=0 Radius=43 StartAngle=0.894703 EndAngle=2.24689
    g38: LineSegment [constr] StartX=-50.5 StartY=2 StartZ=0 EndX=-50.5 EndY=0 EndZ=0
    g39: LineSegment [constr] StartX=-30.5 StartY=6.5 StartZ=0 EndX=-32.5 EndY=6.5 EndZ=0
    g40: LineSegment [constr] StartX=32.5 StartY=2.77908 StartZ=0 EndX=30.5 EndY=2.77908 EndZ=0
    g41: LineSegment StartX=50.5 StartY=2.77908 StartZ=0 EndX=52.5 EndY=2.77908 EndZ=0
    g42: LineSegment [constr] StartX=0.211269 StartY=121.5 StartZ=0 EndX=0.211269 EndY=119.5 EndZ=0
    g43: LineSegment [constr] StartX=-30.5 StartY=6.5 StartZ=0 EndX=-30.5 EndY=9.5 EndZ=0
    g44: ArcOfCircle CenterX=-35.5 CenterY=5 CenterZ=0 NormalX=0 NormalY=0 NormalZ=1 AngleXU=0 Radius=3 StartAngle=4.71239 EndAngle=6.28319
    g45: ArcOfCircle CenterX=35.5 CenterY=5.77908 CenterZ=0 NormalX=0 NormalY=0 NormalZ=1 AngleXU=0 Radius=3 StartAngle=3.14159 EndAngle=4.71239
    g46: LineSegment [constr] StartX=32.5 StartY=5.77908 StartZ=0 EndX=32.5 EndY=2.77908 EndZ=0
    g47: LineSegment [constr] StartX=32.5 StartY=2.77908 StartZ=0 EndX=35.5 EndY=2.77908 EndZ=0
    g48: LineSegment StartX=-52.5 StartY=0 StartZ=0 EndX=-52.5 EndY=2 EndZ=0
    g49: LineSegment StartX=-52.5 StartY=2 StartZ=0 EndX=-50.5 EndY=2 EndZ=0
    g50: LineSegment StartX=52.5 StartY=2.77908 StartZ=0 EndX=52.5 EndY=0 EndZ=0
  constraints (131):
    c: Horizontal(g0)
    c: Coincident(g0,g1)
    c: Vertical(g1)
    c: Coincident(g1,g2)
    c: Coincident(g2,g3)
    c: Vertical(g3)
    c: Coincident(g3,g4)
    c: Horizontal(g4)
    c: Coincident(g4,g5)
    c: Vertical(g5)
    c: Coincident(g8,g0)
    c: Vertical(g8)
    c: PointOnObject(g9,g-2)
    c: Tangent(g9,g6) = -1.5708
    c: Coincident(g10,g7)
    c: Coincident(g10,g6)
    c: Horizontal(g10)
    c: Tangent(g7,g11) = -1.5708
    c: Tangent(g8,g11) = -1.5708
    c: Tangent(g6,g12) = -1.5708
    c: Tangent(g5,g12) = -1.5708
    c: Equal(g12,g11)
    c: Coincident(g13,g8)
    c: Coincident(g13,g5)
    c: Horizontal(g13)
    c: Coincident(g14,g7)
    c: Coincident(g14,g6)
    c: Tangent(g7,g9) = -1.5708
    c: PointOnObject(g0,g-1)
    c: PointOnObject(g4,g-1)
    c: DistanceY(g-1,g2) = 6.5
    c: DistanceX(g1,g2) = 61
    c: Symmetric(g1,g2,g-2)
    c: DistanceX(g0,g4) = 105
    c: DistanceY(g2,g5) = 70
    c: Radius(g9) = 45
    c: Radius(g11) = 30
    c: Coincident(g8,g15)
    c: Vertical(g15)
    c: Coincident(g15,g16)
    c: Horizontal(g16)
    c: Tangent(g16,g9)
    c: Coincident(g16,g17)
    c: Coincident(g17,g5)
    c: Vertical(g17)
    c: DistanceY(g5,g16) = 45
    c: Coincident(g18,g0)
    c: Coincident(g18,g4)
    c: Coincident(g23,g19)
    c: Coincident(g23,g20)
    c: Horizontal(g23)
    c: Coincident(g24,g21)
    c: Coincident(g25,g21)
    c: Coincident(g25,g22)
    c: Horizontal(g25)
    c: Equal(g22,g21)
    c: Equal(g21,g20)
    c: Equal(g20,g19)
    c: Radius(g19) = 1.7
    c: Coincident(g20,g24)
    c: DistanceX(g19,g22) = 50
    c: Symmetric(g20,g21,g-2)
    c: DistanceX(g20,g21) = 15
    c: DistanceY(g0,g19) = 3
    c: Vertical(g26)
    c: Vertical(g29)
    c: Coincident(g29,g30)
    c: Coincident(g31,g32)
    c: Coincident(g32,g33)
    c: Coincident(g34,g26)
    c: Tangent(g26,g35) = 1.5708
    c: Tangent(g27,g35) = 1.5708
    c: Tangent(g28,g36) = 1.5708
    c: Tangent(g29,g36) = 1.5708
    c: Coincident(g37,g9)
    c: Coincident(g37,g27)
    c: PointOnObject(g27,g10)
    c: Coincident(g37,g28)
    c: PointOnObject(g28,g10)
    c: PointOnObject(g26,g13)
    c: PointOnObject(g29,g13)
    c: Horizontal(g32)
    c: Vertical(g33)
    c: Horizontal(g34)
    c: Horizontal(g30)
    c: Vertical(g31)
    c: DistanceX(g0,g26) = 2
    c: DistanceY(g0,g26) = 2
    c: Coincident(g38,g26)
    c: PointOnObject(g38,g0)
    c: Vertical(g38)
    c: Coincident(g39,g1)
    c: PointOnObject(g39,g33)
    c: Horizontal(g39)
    c: Equal(g39,g38)
    c: PointOnObject(g40,g3)
    c: Horizontal(g40)
    c: Coincident(g41,g29)
    c: PointOnObject(g41,g5)
    c: Horizontal(g41)
    c: Equal(g41,g40)
    c: Equal(g40,g38)
    c: PointOnObject(g27,g14)
    c: PointOnObject(g28,g14)
    c: PointOnObject(g42,g9)
    c: PointOnObject(g42,g37)
    c: Vertical(g42)
    c: DistanceY(g42,g42) = 2
    c: Coincident(g43,g1)
    c: PointOnObject(g43,g32)
    c: Vertical(g43)
    c: DistanceY(g43,g43) = 3
    c: Tangent(g34,g44) = 1.5708
    c: Tangent(g33,g44) = 1.5708
    c: Radius(g44) = 3
    c: Tangent(g31,g45) = 1.5708
    c: Tangent(g30,g45) = 1.5708
    c: Coincident(g46,g31)
    c: Coincident(g46,g40)
    c: Coincident(g47,g40)
    c: Coincident(g47,g30)
    c: Radius(g45) = 3
    c: Horizontal(g47)
    c: Vertical(g46)
    c: Coincident(g48,g0)
    c: Vertical(g48)
    c: Coincident(g49,g48)
    c: Coincident(g49,g34)
    c: Horizontal(g49)
    c: Coincident(g50,g41)
    c: Coincident(g50,g4)
FEATURE [PartDesign::Pad] Pad007  label="Timone Porta Batterie003"
  BaseFeature = -> Pad006
  Length = 5
  Length2 = 100
  Profile = -> Sketch026
  Type = 0
FEATURE [Sketcher::SketchObject] Sketch027
  MapMode = 5
  Placement = pos=(0,9.5,0) rot=(0,0.707107,0.707107;3.14159rad)
  Support = -> [Pad007]
  sketch-geometry (12):
    g0: Circle CenterX=-14.882 CenterY=23 CenterZ=0 NormalX=0 NormalY=0 NormalZ=1 AngleXU=0 Radius=1.7
    g1: Circle CenterX=0 CenterY=23 CenterZ=0 NormalX=0 NormalY=0 NormalZ=1 AngleXU=0 Radius=1.7
    g2: Circle CenterX=15.118 CenterY=23 CenterZ=0 NormalX=0 NormalY=0 NormalZ=1 AngleXU=0 Radius=1.7
    g3: Circle CenterX=15.118 CenterY=7 CenterZ=0 NormalX=0 NormalY=0 NormalZ=1 AngleXU=0 Radius=1.7
    g4: Circle CenterX=0 CenterY=7 CenterZ=0 NormalX=0 NormalY=0 NormalZ=1 AngleXU=0 Radius=1.7
    g5: Circle CenterX=-14.882 CenterY=7 CenterZ=0 NormalX=0 NormalY=0 NormalZ=1 AngleXU=0 Radius=1.7
    g6: LineSegment [constr] StartX=-14.882 StartY=23 StartZ=0 EndX=0 EndY=23 EndZ=0
    g7: LineSegment [constr] StartX=0 StartY=23 StartZ=0 EndX=15.118 EndY=23 EndZ=0
    g8: LineSegment [constr] StartX=15.118 StartY=23 StartZ=0 EndX=15.118 EndY=7 EndZ=0
    g9: LineSegment [constr] StartX=15.118 StartY=7 StartZ=0 EndX=0 EndY=7 EndZ=0
    g10: LineSegment [constr] StartX=0 StartY=7 StartZ=0 EndX=-14.882 EndY=7 EndZ=0
    g11: LineSegment [constr] StartX=-14.882 StartY=7 StartZ=0 EndX=-14.882 EndY=23 EndZ=0
  constraints (29):
    c: PointOnObject(g1,g-2)
    c: PointOnObject(g4,g-2)
    c: Coincident(g6,g0)
    c: Coincident(g6,g1)
    c: Horizontal(g6)
    c: Coincident(g6,g7)
    c: Coincident(g7,g2)
    c: Horizontal(g7)
    c: Coincident(g7,g8)
    c: Coincident(g8,g3)
    c: Vertical(g8)
    c: Coincident(g8,g9)
    c: Coincident(g9,g4)
    c: Coincident(g9,g10)
    c: Coincident(g10,g5)
    c: Horizontal(g10)
    c: Coincident(g10,g11)
    c: Coincident(g11,g6)
    c: Vertical(g11)
    c: Horizontal(g9)
    c: DistanceX(g0,g2) = 30
    c: DistanceY(g5,g0) = 16
    c: Equal(g0,g1)
    c: Equal(g1,g2)
    c: Equal(g2,g3)
    c: Equal(g3,g4)
    c: Equal(g4,g5)
    c: Radius(g0) = 1.7
    c: DistanceY(g-1,g5) = 7
FEATURE [PartDesign::Pocket] Pocket018  label="Timone Porta Batterie004"
  BaseFeature = -> Pad007
  Length = 10
  Length2 = 100
  Profile = -> Sketch027
  Type = 0
FEATURE [PartDesign::Body] Body004  label="TimonePortaBatterie"
  Group = -> [Sketch023,Pad004,Sketch024,Pad005,Sketch025,Pad006,Sketch026,Pad007,Sketch027,Pocket018]
  Origin = -> Origin009
  Tip = -> Pocket018
FEATURE [App::Part] Part004  label="Timone Porta Batterie"
  Group = -> [Body004]
  Origin = -> Origin008
  Placement = pos=(0,25,-15) rot=(0,0,1;0rad)
FEATURE [Sketcher::SketchObject] Sketch028  label="AsseAcciaio"
  MapMode = 5
  Placement = pos=(42.6,0,0) rot=(0.707107,0,0.707107;3.14159rad)
  Support = -> [Pocket015]
  sketch-geometry (1):
    g0: Circle CenterX=0 CenterY=0 CenterZ=0 NormalX=0 NormalY=0 NormalZ=1 AngleXU=0 Radius=1
  constraints (2):
    c: Coincident(g0,g-1)
    c: Radius(g0) = 1
FEATURE [PartDesign::Pocket] Pocket019  label="RuoteDa90asse017"
  BaseFeature = -> Pocket015
  Length = 100
  Length2 = 100
  Placement = pos=(0,0,0) rot=(1,0,0;1.5708rad)
  Profile = -> Sketch028
  Type = 0
FEATURE [PartDesign::Body] Body001  label="RuoteDa90asse8"
  Group = -> [Sketch011,Revolution,Sketch013,Sketch017,Pocket014,Fillet001,Pocket015,Sketch028,Pocket019]
  Origin = -> Origin003
  Tip = -> Pocket019
FEATURE [App::Part] Part001  label="Ruote da 90 asse 8SX"
  Group = -> [Body001]
  Origin = -> Origin002
  Placement = pos=(-27,0,0) rot=(0,0,1;3.14159rad)
FEATURE [Sketcher::SketchObject] Sketch029  label="SupportoSfera001"
  MapMode = 5
  Support = -> [XY_Plane011]
  sketch-geometry (9):
    g0: Circle CenterX=0 CenterY=-1e-16 CenterZ=0 NormalX=0 NormalY=0 NormalZ=1 AngleXU=0 Radius=16
    g1: Circle CenterX=0 CenterY=-1e-16 CenterZ=0 NormalX=0 NormalY=0 NormalZ=1 AngleXU=0 Radius=10
    g2: LineSegment [constr] StartX=10.3923 StartY=-6 StartZ=0 EndX=0 EndY=12 EndZ=0
    g3: LineSegment [constr] StartX=0 StartY=12 StartZ=0 EndX=-10.3923 EndY=-6 EndZ=0
    g4: LineSegment [constr] StartX=-10.3923 StartY=-6 StartZ=0 EndX=10.3923 EndY=-6 EndZ=0
    g5: Circle [constr] CenterX=0 CenterY=-1e-16 CenterZ=0 NormalX=0 NormalY=0 NormalZ=1 AngleXU=0 Radius=12
    g6: Circle CenterX=0 CenterY=12 CenterZ=0 NormalX=0 NormalY=0 NormalZ=1 AngleXU=0 Radius=1.7
    g7: Circle CenterX=-10.3923 CenterY=-6 CenterZ=0 NormalX=0 NormalY=0 NormalZ=1 AngleXU=0 Radius=1.7
    g8: Circle CenterX=10.3923 CenterY=-6 CenterZ=0 NormalX=0 NormalY=0 NormalZ=1 AngleXU=0 Radius=1.7
  constraints (21):
    c: Coincident(g0,g-1)
    c: Coincident(g1,g0)
    c: Coincident(g2,g3)
    c: Coincident(g3,g4)
    c: Coincident(g4,g2)
    c: Equal(g2,g3)
    c: Equal(g2,g4)
    c: PointOnObject(g2,g5)
    c: PointOnObject(g3,g5)
    c: PointOnObject(g4,g5)
    c: Coincident(g5,g0)
    c: PointOnObject(g2,g-2)
    c: Radius(g0) = 16
    c: Radius(g5) = 12
    c: Coincident(g6,g2)
    c: Coincident(g7,g3)
    c: Coincident(g8,g2)
    c: Equal(g7,g8)
    c: Radius(g6) = 1.7
    c: Equal(g6,g7)
    c: Radius(g1) = 10
FEATURE [PartDesign::Pad] Pad008
  Length = 7
  Length2 = 100
  Profile = -> Sketch029
  Type = 0
FEATURE [Sketcher::SketchObject] Sketch030  label="SupportoSfera002"
  MapMode = 5
  Placement = pos=(0,0,7) rot=(0,0,1;0rad)
  Support = -> [Pad008]
  sketch-geometry (21):
    g0: Circle [constr] CenterX=0 CenterY=-1e-16 CenterZ=0 NormalX=0 NormalY=0 NormalZ=1 AngleXU=0 Radius=16
    g1: Circle [constr] CenterX=0 CenterY=-1e-16 CenterZ=0 NormalX=0 NormalY=0 NormalZ=1 AngleXU=0 Radius=10
    g2: LineSegment [constr] StartX=10.3923 StartY=-6 StartZ=0 EndX=0 EndY=12 EndZ=0
    g3: LineSegment [constr] StartX=0 StartY=12 StartZ=0 EndX=-10.3923 EndY=-6 EndZ=0
    g4: LineSegment [constr] StartX=-10.3923 StartY=-6 StartZ=0 EndX=10.3923 EndY=-6 EndZ=0
    g5: Circle [constr] CenterX=0 CenterY=-1e-16 CenterZ=0 NormalX=0 NormalY=0 NormalZ=1 AngleXU=0 Radius=12
    g6: Circle [constr] CenterX=0 CenterY=12 CenterZ=0 NormalX=0 NormalY=0 NormalZ=1 AngleXU=0 Radius=1.7
    g7: Circle [constr] CenterX=-10.3923 CenterY=-6 CenterZ=0 NormalX=0 NormalY=0 NormalZ=1 AngleXU=0 Radius=1.7
    g8: Circle [constr] CenterX=10.3923 CenterY=-6 CenterZ=0 NormalX=0 NormalY=0 NormalZ=1 AngleXU=0 Radius=1.7
    g9: ArcOfCircle CenterX=-12.5 CenterY=0 CenterZ=0 NormalX=0 NormalY=0 NormalZ=1 AngleXU=0 Radius=16 StartAngle=1.5708 EndAngle=4.71239
    g10: ArcOfCircle CenterX=12.5 CenterY=3e-16 CenterZ=0 NormalX=0 NormalY=0 NormalZ=1 AngleXU=0 Radius=16 StartAngle=4.71239 EndAngle=7.85398
    g11: LineSegment StartX=-12.5 StartY=-16 StartZ=0 EndX=12.5 EndY=-16 EndZ=0
    g12: LineSegment StartX=-12.5 StartY=16 StartZ=0 EndX=12.5 EndY=16 EndZ=0
    g13: Circle [constr] CenterX=-17.4858 CenterY=7.64555 CenterZ=0 NormalX=0 NormalY=0 NormalZ=1 AngleXU=0 Radius=1.8
    g14: Circle [constr] CenterX=-17.4858 CenterY=-7.64555 CenterZ=0 NormalX=0 NormalY=0 NormalZ=1 AngleXU=0 Radius=1.8
    g15: Circle [constr] CenterX=17.4858 CenterY=-7.64555 CenterZ=0 NormalX=0 NormalY=0 NormalZ=1 AngleXU=0 Radius=1.8
    g16: Circle [constr] CenterX=17.4858 CenterY=7.64555 CenterZ=0 NormalX=0 NormalY=0 NormalZ=1 AngleXU=0 Radius=1.8
    g17: LineSegment [constr] StartX=-17.4858 StartY=7.64555 StartZ=0 EndX=17.4858 EndY=7.64555 EndZ=0
    g18: LineSegment [constr] StartX=17.4858 StartY=7.64555 StartZ=0 EndX=17.4858 EndY=-7.64555 EndZ=0
    g19: LineSegment [constr] StartX=17.4858 StartY=-7.64555 StartZ=0 EndX=-17.4858 EndY=-7.64555 EndZ=0
    g20: LineSegment [constr] StartX=-17.4858 StartY=-7.64555 StartZ=0 EndX=-17.4858 EndY=7.64555 EndZ=0
  constraints (46):
    c: Coincident(g0,g-1)
    c: Coincident(g1,g0)
    c: Coincident(g2,g3)
    c: Coincident(g3,g4)
    c: Coincident(g4,g2)
    c: Equal(g2,g3)
    c: Equal(g2,g4)
    c: PointOnObject(g2,g5)
    c: PointOnObject(g3,g5)
    c: PointOnObject(g4,g5)
    c: Coincident(g5,g0)
    c: PointOnObject(g2,g-2)
    c: Radius(g0) = 16
    c: Radius(g5) = 12
    c: Coincident(g6,g2)
    c: Coincident(g7,g3)
    c: Coincident(g8,g2)
    c: Equal(g7,g8)
    c: Radius(g6) = 1.7
    c: Equal(g6,g7)
    c: Radius(g1) = 10
    c: Tangent(g9,g12) = 1.5708
    c: Tangent(g9,g11) = -1.5708
    c: Tangent(g11,g10) = -1.5708
    c: Tangent(g12,g10) = 1.5708
    c: Horizontal(g11)
    c: PointOnObject(g9,g-1)
    c: Symmetric(g10,g9,g-2)
    c: DistanceY(g10,g10) = 32
    c: DistanceX(g9,g10) = 25
    c: Coincident(g17,g18)
    c: Coincident(g18,g19)
    c: Coincident(g19,g20)
    c: Coincident(g20,g17)
    c: Horizontal(g19)
    c: Vertical(g18)
    c: Coincident(g17,g13)
    c: Coincident(g18,g15)
    c: Coincident(g19,g14)
    c: Coincident(g17,g16)
    c: Equal(g16,g13)
    c: Equal(g13,g14)
    c: Symmetric(g13,g16,g-2)
    c: Symmetric(g13,g14,g-1)
    c: Equal(g15,g16)
    c: Radius(g13) = 1.8
FEATURE [PartDesign::Pad] Pad009
  BaseFeature = -> Pad008
  Length = 15
  Length2 = 100
  Profile = -> Sketch030
  Type = 0
FEATURE [Sketcher::SketchObject] Sketch031  label="SupportoSfera003"
  MapMode = 5
  Placement = pos=(0,0,22) rot=(0,0,1;0rad)
  Support = -> [Pad009]
  sketch-geometry (21):
    g0: Circle [constr] CenterX=0 CenterY=-1e-16 CenterZ=0 NormalX=0 NormalY=0 NormalZ=1 AngleXU=0 Radius=16
    g1: Circle [constr] CenterX=0 CenterY=-1e-16 CenterZ=0 NormalX=0 NormalY=0 NormalZ=1 AngleXU=0 Radius=10
    g2: LineSegment [constr] StartX=10.3923 StartY=-6 StartZ=0 EndX=0 EndY=12 EndZ=0
    g3: LineSegment [constr] StartX=0 StartY=12 StartZ=0 EndX=-10.3923 EndY=-6 EndZ=0
    g4: LineSegment [constr] StartX=-10.3923 StartY=-6 StartZ=0 EndX=10.3923 EndY=-6 EndZ=0
    g5: Circle [constr] CenterX=0 CenterY=-1e-16 CenterZ=0 NormalX=0 NormalY=0 NormalZ=1 AngleXU=0 Radius=12
    g6: Circle [constr] CenterX=0 CenterY=12 CenterZ=0 NormalX=0 NormalY=0 NormalZ=1 AngleXU=0 Radius=1.7
    g7: Circle [constr] CenterX=-10.3923 CenterY=-6 CenterZ=0 NormalX=0 NormalY=0 NormalZ=1 AngleXU=0 Radius=1.7
    g8: Circle [constr] CenterX=10.3923 CenterY=-6 CenterZ=0 NormalX=0 NormalY=0 NormalZ=1 AngleXU=0 Radius=1.7
    g9: ArcOfCircle [constr] CenterX=-12.5 CenterY=0 CenterZ=0 NormalX=0 NormalY=0 NormalZ=1 AngleXU=0 Radius=16 StartAngle=1.5708 EndAngle=4.71239
    g10: ArcOfCircle [constr] CenterX=12.5 CenterY=3e-16 CenterZ=0 NormalX=0 NormalY=0 NormalZ=1 AngleXU=0 Radius=16 StartAngle=4.71239 EndAngle=7.85398
    g11: LineSegment [constr] StartX=-12.5 StartY=-16 StartZ=0 EndX=12.5 EndY=-16 EndZ=0
    g12: LineSegment [constr] StartX=-12.5 StartY=16 StartZ=0 EndX=12.5 EndY=16 EndZ=0
    g13: Circle CenterX=-17.4918 CenterY=7.55431 CenterZ=0 NormalX=0 NormalY=0 NormalZ=1 AngleXU=0 Radius=1.8
    g14: Circle CenterX=-17.4918 CenterY=-7.55431 CenterZ=0 NormalX=0 NormalY=0 NormalZ=1 AngleXU=0 Radius=1.8
    g15: Circle CenterX=17.4918 CenterY=-7.55431 CenterZ=0 NormalX=0 NormalY=0 NormalZ=1 AngleXU=0 Radius=1.8
    g16: Circle CenterX=17.4918 CenterY=7.55431 CenterZ=0 NormalX=0 NormalY=0 NormalZ=1 AngleXU=0 Radius=1.8
    g17: LineSegment [constr] StartX=-17.4918 StartY=7.55431 StartZ=0 EndX=17.4918 EndY=7.55431 EndZ=0
    g18: LineSegment [constr] StartX=17.4918 StartY=7.55431 StartZ=0 EndX=17.4918 EndY=-7.55431 EndZ=0
    g19: LineSegment [constr] StartX=17.4918 StartY=-7.55431 StartZ=0 EndX=-17.4918 EndY=-7.55431 EndZ=0
    g20: LineSegment [constr] StartX=-17.4918 StartY=-7.55431 StartZ=0 EndX=-17.4918 EndY=7.55431 EndZ=0
  constraints (46):
    c: Coincident(g0,g-1)
    c: Coincident(g1,g0)
    c: Coincident(g2,g3)
    c: Coincident(g3,g4)
    c: Coincident(g4,g2)
    c: Equal(g2,g3)
    c: Equal(g2,g4)
    c: PointOnObject(g2,g5)
    c: PointOnObject(g3,g5)
    c: PointOnObject(g4,g5)
    c: Coincident(g5,g0)
    c: PointOnObject(g2,g-2)
    c: Radius(g0) = 16
    c: Radius(g5) = 12
    c: Coincident(g6,g2)
    c: Coincident(g7,g3)
    c: Coincident(g8,g2)
    c: Equal(g7,g8)
    c: Radius(g6) = 1.7
    c: Equal(g6,g7)
    c: Radius(g1) = 10
    c: Tangent(g9,g12) = 1.5708
    c: Tangent(g9,g11) = -1.5708
    c: Tangent(g11,g10) = -1.5708
    c: Tangent(g12,g10) = 1.5708
    c: Horizontal(g11)
    c: PointOnObject(g9,g-1)
    c: Symmetric(g10,g9,g-2)
    c: DistanceY(g10,g10) = 32
    c: DistanceX(g9,g10) = 25
    c: Coincident(g17,g18)
    c: Coincident(g18,g19)
    c: Coincident(g19,g20)
    c: Coincident(g20,g17)
    c: Horizontal(g19)
    c: Vertical(g18)
    c: Coincident(g17,g13)
    c: Coincident(g18,g15)
    c: Coincident(g19,g14)
    c: Coincident(g17,g16)
    c: Equal(g16,g13)
    c: Equal(g13,g14)
    c: Symmetric(g13,g16,g-2)
    c: Symmetric(g13,g14,g-1)
    c: Equal(g15,g16)
    c: Radius(g13) = 1.8
FEATURE [PartDesign::Pocket] Pocket020
  BaseFeature = -> Pad009
  Length = 30
  Length2 = 100
  Profile = -> Sketch031
  Type = 0
FEATURE [Sketcher::SketchObject] Sketch032
  MapMode = 5
  Placement = pos=(0,16,0) rot=(0,0.707107,0.707107;3.14159rad)
  Support = -> [Pocket020]
  sketch-geometry (15):
    g0: LineSegment StartX=-23 StartY=21.7525 StartZ=0 EndX=23 EndY=21.7525 EndZ=0
    g1: LineSegment StartX=23 StartY=21.7525 StartZ=0 EndX=23 EndY=0.077331 EndZ=0
    g2: LineSegment StartX=23 StartY=0.077331 StartZ=0 EndX=-23 EndY=0.077331 EndZ=0
    g3: LineSegment StartX=-23 StartY=0.077331 StartZ=0 EndX=-23 EndY=21.7525 EndZ=0
    g4: LineSegment [constr] StartX=-72.7015 StartY=-8.2472 StartZ=0 EndX=89.5485 EndY=-8.2472 EndZ=0
    g5: ArcOfCircle CenterX=-17 CenterY=16 CenterZ=0 NormalX=0 NormalY=0 NormalZ=1 AngleXU=0 Radius=0.4 StartAngle=-5.3e-15 EndAngle=3.14159
    g6: ArcOfCircle CenterX=-17 CenterY=4 CenterZ=0 NormalX=0 NormalY=0 NormalZ=1 AngleXU=0 Radius=0.4 StartAngle=3.14159 EndAngle=6.28319
    g7: LineSegment StartX=-17.4 StartY=16 StartZ=0 EndX=-17.4 EndY=4 EndZ=0
    g8: LineSegment StartX=-16.6 StartY=16 StartZ=0 EndX=-16.6 EndY=4 EndZ=0
    g9: ArcOfCircle CenterX=17 CenterY=16 CenterZ=0 NormalX=0 NormalY=0 NormalZ=1 AngleXU=0 Radius=0.4 StartAngle=0 EndAngle=3.14159
    g10: ArcOfCircle CenterX=17 CenterY=4 CenterZ=0 NormalX=0 NormalY=0 NormalZ=1 AngleXU=0 Radius=0.4 StartAngle=3.14159 EndAngle=6.28319
    g11: LineSegment StartX=16.6 StartY=16 StartZ=0 EndX=16.6 EndY=4 EndZ=0
    g12: LineSegment StartX=17.4 StartY=16 StartZ=0 EndX=17.4 EndY=4 EndZ=0
    g13: LineSegment [constr] StartX=-16.6 StartY=16 StartZ=0 EndX=16.6 EndY=16 EndZ=0
    g14: LineSegment [constr] StartX=-16.6 StartY=4 StartZ=0 EndX=16.6 EndY=4 EndZ=0
  constraints (33):
    c: Coincident(g0,g1)
    c: Coincident(g1,g2)
    c: Coincident(g2,g3)
    c: Coincident(g3,g0)
    c: Horizontal(g0)
    c: Vertical(g1)
    c: Vertical(g3)
    c: Horizontal(g4)
    c: Symmetric(g2,g1,g-2)
    c: DistanceX(g2,g1) = 46
    c: Tangent(g5,g8) = 1.5708
    c: Tangent(g5,g7) = -1.5708
    c: Tangent(g7,g6) = -1.5708
    c: Tangent(g8,g6) = 1.5708
    c: Vertical(g7)
    c: Equal(g5,g6)
    c: Tangent(g9,g12) = 1.5708
    c: Tangent(g9,g11) = -1.5708
    c: Tangent(g11,g10) = -1.5708
    c: Tangent(g12,g10) = 1.5708
    c: Vertical(g11)
    c: Equal(g9,g10)
    c: Equal(g9,g5)
    c: Coincident(g13,g5)
    c: Coincident(g13,g9)
    c: Horizontal(g13)
    c: Coincident(g14,g6)
    c: Coincident(g14,g10)
    c: Symmetric(g10,g6,g-2)
    c: DistanceX(g6,g10) = 34
    c: Radius(g6) = 0.4
    c: DistanceY(g6,g5) = 12
    c: DistanceY(g-1,g6) = 4
FEATURE [PartDesign::Pad] Pad010
  BaseFeature = -> Pocket020
  Length = 5
  Length2 = 100
  Profile = -> Sketch032
  Type = 0
FEATURE [PartDesign::Body] Body005  label="SupportoSfera"
  Group = -> [Sketch029,Pad008,Sketch030,Pad009,Sketch031,Pocket020,Sketch032,Pad010]
  Origin = -> Origin011
  Tip = -> Pad010
FEATURE [App::Part] Part005  label="Supporto Sfera"
  Group = -> [Body005]
  Origin = -> Origin010
  Placement = pos=(0,115.5,-37) rot=(0,0,1;0rad)
